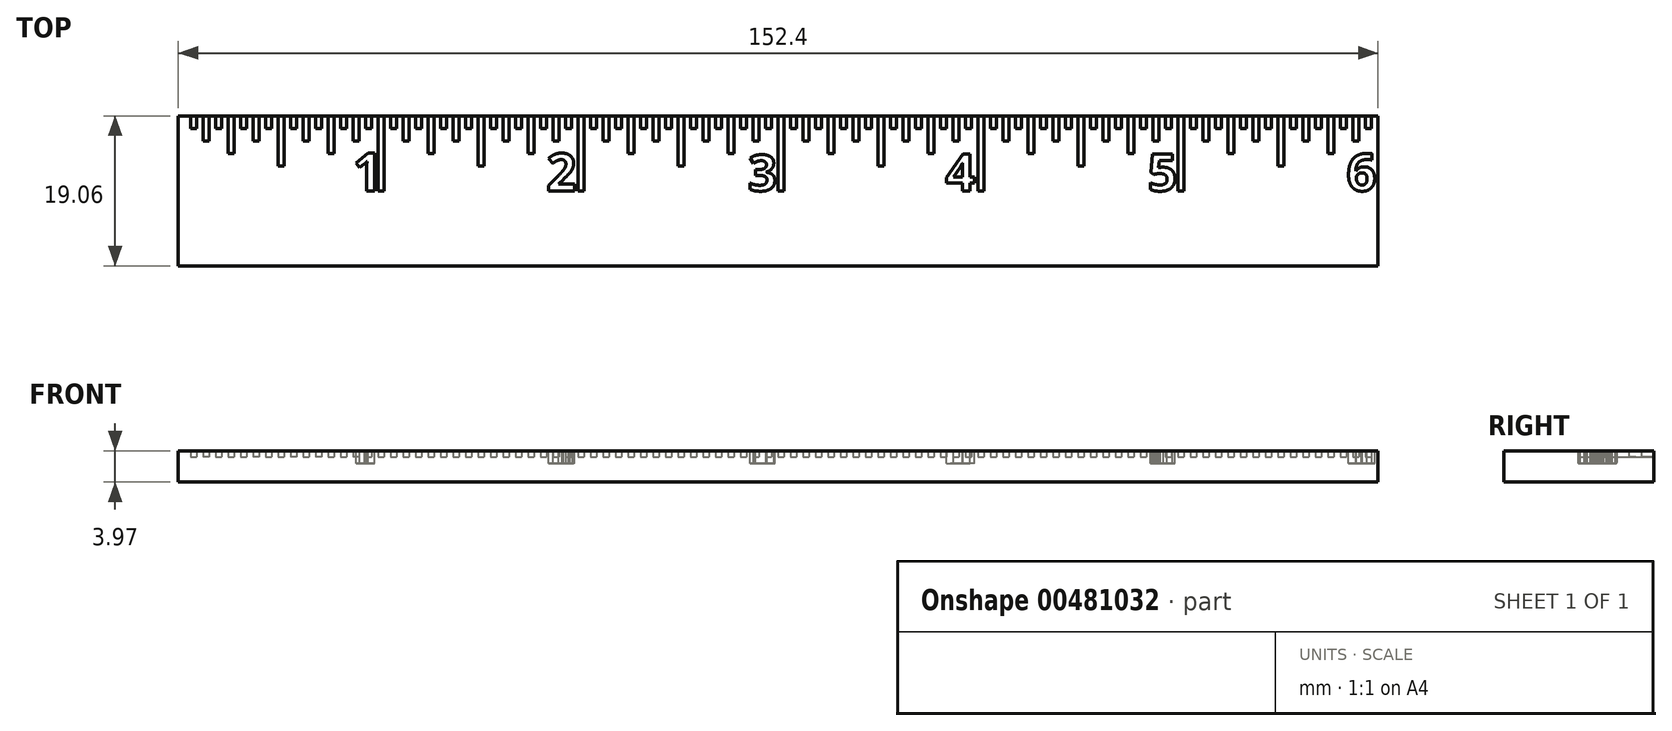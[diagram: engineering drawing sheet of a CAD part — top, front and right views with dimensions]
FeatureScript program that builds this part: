
annotation { "Feature Type Name" : "Feature", "Feature Type Description" : "" }
export const myFeature = defineFeature(function(context is Context, id is Id, definition is map)
    precondition{}
    {
        {
            var Q0;
            Q0=qCreatedBy(makeId("Top.planeOp"),FACE);
            var sketch = newSketch(context, id + "F0", { "sketchPlane" : qUnion([Q0])});
            skLineSegment(sketch, "E0.bottom", {"start": v(-76.2, 9.52) * mm, "end": v(76.2, 9.52) * mm});
            skLineSegment(sketch, "E0.top", {"start": v(-76.2, -9.52) * mm, "end": v(76.2, -9.52) * mm});
            skLineSegment(sketch, "E0.left", {"start": v(-76.2, 9.52) * mm, "end": v(-76.2, -9.52) * mm});
            skLineSegment(sketch, "E0.right", {"start": v(76.2, 9.52) * mm, "end": v(76.2, -9.52) * mm});
            skPoint(sketch, "E0.middle", {"position": v(0, 0) * mm});
            skSolve(sketch);
        }
        {
            var Q0;
            Q0 = qSketchRegion(id + "F0", true);
            extrude(context, id + "F1", {"entities" : qUnion([Q0]), "depth" : 3.17 * mm});
        }
        {
            var Q0;
            Q0=makeQuery(id+"F1.opExtrude","CAP_FACE",FACE,{"disambiguationData":[OSD([sQuery(id+"F0.wireOp",EDGE,"E0.bottom"),sQuery(id+"F0.wireOp",EDGE,"E0.top"),sQuery(id+"F0.wireOp",EDGE,"E0.left"),sQuery(id+"F0.wireOp",EDGE,"E0.right")])],"isStart":false});
            var sketch = newSketch(context, id + "F2", { "sketchPlane" : qUnion([Q0])});
            skLineSegment(sketch, "E1", {"start": v(-50.8, 9.52) * mm, "end": v(-50.8, 0) * mm});
            skLineSegment(sketch, "E2.1.0.0", {"start": v(-25.4, 9.52) * mm, "end": v(-25.4, 0) * mm});
            skLineSegment(sketch, "E2.2.0.0", {"start": v(0, 9.52) * mm, "end": v(0, 0) * mm});
            skLineSegment(sketch, "E2.3.0.0", {"start": v(25.4, 9.52) * mm, "end": v(25.4, 0) * mm});
            skLineSegment(sketch, "E2.4.0.0", {"start": v(50.8, 9.52) * mm, "end": v(50.8, 0) * mm});
            skLineSegment(sketch, "E2.direction1", {"start": v(-50.8, 0) * mm, "end": v(-25.4, 0) * mm, "construction": true});
            skLineSegment(sketch, "E3", {"start": v(-63.5, 9.52) * mm, "end": v(-63.5, 3.17) * mm});
            skLineSegment(sketch, "E4.1.0.0", {"start": v(-38.1, 9.52) * mm, "end": v(-38.1, 3.17) * mm});
            skLineSegment(sketch, "E4.2.0.0", {"start": v(-12.7, 9.52) * mm, "end": v(-12.7, 3.17) * mm});
            skLineSegment(sketch, "E4.3.0.0", {"start": v(12.7, 9.52) * mm, "end": v(12.7, 3.17) * mm});
            skLineSegment(sketch, "E4.4.0.0", {"start": v(38.1, 9.52) * mm, "end": v(38.1, 3.17) * mm});
            skLineSegment(sketch, "E4.5.0.0", {"start": v(63.5, 9.52) * mm, "end": v(63.5, 3.17) * mm});
            skLineSegment(sketch, "E4.direction1", {"start": v(-63.5, 3.17) * mm, "end": v(-38.1, 3.17) * mm, "construction": true});
            skLineSegment(sketch, "E5", {"start": v(-69.85, 9.52) * mm, "end": v(-69.85, 4.76) * mm});
            skLineSegment(sketch, "E6.1.0.0", {"start": v(-57.15, 9.52) * mm, "end": v(-57.15, 4.76) * mm});
            skLineSegment(sketch, "E6.2.0.0", {"start": v(-44.45, 9.52) * mm, "end": v(-44.45, 4.76) * mm});
            skLineSegment(sketch, "E6.3.0.0", {"start": v(-31.75, 9.52) * mm, "end": v(-31.75, 4.76) * mm});
            skLineSegment(sketch, "E6.4.0.0", {"start": v(-19.05, 9.52) * mm, "end": v(-19.05, 4.76) * mm});
            skLineSegment(sketch, "E6.5.0.0", {"start": v(-6.35, 9.52) * mm, "end": v(-6.35, 4.76) * mm});
            skLineSegment(sketch, "E6.6.0.0", {"start": v(6.35, 9.52) * mm, "end": v(6.35, 4.76) * mm});
            skLineSegment(sketch, "E6.7.0.0", {"start": v(19.05, 9.52) * mm, "end": v(19.05, 4.76) * mm});
            skLineSegment(sketch, "E6.8.0.0", {"start": v(31.75, 9.52) * mm, "end": v(31.75, 4.76) * mm});
            skLineSegment(sketch, "E6.9.0.0", {"start": v(44.45, 9.52) * mm, "end": v(44.45, 4.76) * mm});
            skLineSegment(sketch, "E6.10.0.0", {"start": v(57.15, 9.52) * mm, "end": v(57.15, 4.76) * mm});
            skLineSegment(sketch, "E6.11.0.0", {"start": v(69.85, 9.52) * mm, "end": v(69.85, 4.76) * mm});
            skLineSegment(sketch, "E6.direction1", {"start": v(-69.85, 4.76) * mm, "end": v(-57.15, 4.76) * mm, "construction": true});
            skLineSegment(sketch, "E7", {"start": v(-73.03, 9.52) * mm, "end": v(-73.03, 6.35) * mm});
            skLineSegment(sketch, "E8.1.0.0", {"start": v(-66.68, 9.52) * mm, "end": v(-66.68, 6.35) * mm});
            skLineSegment(sketch, "E8.2.0.0", {"start": v(-60.33, 9.52) * mm, "end": v(-60.33, 6.35) * mm});
            skLineSegment(sketch, "E8.3.0.0", {"start": v(-53.98, 9.52) * mm, "end": v(-53.98, 6.35) * mm});
            skLineSegment(sketch, "E8.4.0.0", {"start": v(-47.63, 9.52) * mm, "end": v(-47.63, 6.35) * mm});
            skLineSegment(sketch, "E8.5.0.0", {"start": v(-41.28, 9.52) * mm, "end": v(-41.28, 6.35) * mm});
            skLineSegment(sketch, "E8.6.0.0", {"start": v(-34.93, 9.52) * mm, "end": v(-34.93, 6.35) * mm});
            skLineSegment(sketch, "E8.7.0.0", {"start": v(-28.58, 9.52) * mm, "end": v(-28.58, 6.35) * mm});
            skLineSegment(sketch, "E8.8.0.0", {"start": v(-22.23, 9.52) * mm, "end": v(-22.23, 6.35) * mm});
            skLineSegment(sketch, "E8.9.0.0", {"start": v(-15.88, 9.52) * mm, "end": v(-15.88, 6.35) * mm});
            skLineSegment(sketch, "E8.10.0.0", {"start": v(-9.53, 9.52) * mm, "end": v(-9.53, 6.35) * mm});
            skLineSegment(sketch, "E8.11.0.0", {"start": v(-3.18, 9.52) * mm, "end": v(-3.18, 6.35) * mm});
            skLineSegment(sketch, "E8.12.0.0", {"start": v(3.17, 9.52) * mm, "end": v(3.17, 6.35) * mm});
            skLineSegment(sketch, "E8.13.0.0", {"start": v(9.52, 9.52) * mm, "end": v(9.52, 6.35) * mm});
            skLineSegment(sketch, "E8.14.0.0", {"start": v(15.87, 9.52) * mm, "end": v(15.87, 6.35) * mm});
            skLineSegment(sketch, "E8.15.0.0", {"start": v(22.22, 9.52) * mm, "end": v(22.22, 6.35) * mm});
            skLineSegment(sketch, "E8.16.0.0", {"start": v(28.57, 9.52) * mm, "end": v(28.57, 6.35) * mm});
            skLineSegment(sketch, "E8.17.0.0", {"start": v(34.92, 9.52) * mm, "end": v(34.92, 6.35) * mm});
            skLineSegment(sketch, "E8.18.0.0", {"start": v(41.27, 9.52) * mm, "end": v(41.27, 6.35) * mm});
            skLineSegment(sketch, "E8.19.0.0", {"start": v(47.62, 9.52) * mm, "end": v(47.62, 6.35) * mm});
            skLineSegment(sketch, "E8.20.0.0", {"start": v(53.97, 9.52) * mm, "end": v(53.97, 6.35) * mm});
            skLineSegment(sketch, "E8.21.0.0", {"start": v(60.32, 9.52) * mm, "end": v(60.32, 6.35) * mm});
            skLineSegment(sketch, "E8.22.0.0", {"start": v(66.67, 9.52) * mm, "end": v(66.67, 6.35) * mm});
            skLineSegment(sketch, "E8.23.0.0", {"start": v(73.02, 9.52) * mm, "end": v(73.02, 6.35) * mm});
            skLineSegment(sketch, "E8.direction1", {"start": v(-73.03, 6.35) * mm, "end": v(-66.68, 6.35) * mm, "construction": true});
            skLineSegment(sketch, "E9", {"start": v(-74.61, 9.52) * mm, "end": v(-74.61, 7.94) * mm});
            skLineSegment(sketch, "E10.1.0.0", {"start": v(-71.44, 9.52) * mm, "end": v(-71.44, 7.94) * mm});
            skLineSegment(sketch, "E10.2.0.0", {"start": v(-68.26, 9.52) * mm, "end": v(-68.26, 7.94) * mm});
            skLineSegment(sketch, "E10.3.0.0", {"start": v(-65.09, 9.52) * mm, "end": v(-65.09, 7.94) * mm});
            skLineSegment(sketch, "E10.4.0.0", {"start": v(-61.91, 9.52) * mm, "end": v(-61.91, 7.94) * mm});
            skLineSegment(sketch, "E10.5.0.0", {"start": v(-58.74, 9.52) * mm, "end": v(-58.74, 7.94) * mm});
            skLineSegment(sketch, "E10.6.0.0", {"start": v(-55.56, 9.52) * mm, "end": v(-55.56, 7.94) * mm});
            skLineSegment(sketch, "E10.7.0.0", {"start": v(-52.39, 9.52) * mm, "end": v(-52.39, 7.94) * mm});
            skLineSegment(sketch, "E10.8.0.0", {"start": v(-49.21, 9.52) * mm, "end": v(-49.21, 7.94) * mm});
            skLineSegment(sketch, "E10.9.0.0", {"start": v(-46.04, 9.52) * mm, "end": v(-46.04, 7.94) * mm});
            skLineSegment(sketch, "E10.10.0.0", {"start": v(-42.86, 9.52) * mm, "end": v(-42.86, 7.94) * mm});
            skLineSegment(sketch, "E10.11.0.0", {"start": v(-39.69, 9.52) * mm, "end": v(-39.69, 7.94) * mm});
            skLineSegment(sketch, "E10.12.0.0", {"start": v(-36.51, 9.52) * mm, "end": v(-36.51, 7.94) * mm});
            skLineSegment(sketch, "E10.13.0.0", {"start": v(-33.34, 9.52) * mm, "end": v(-33.34, 7.94) * mm});
            skLineSegment(sketch, "E10.14.0.0", {"start": v(-30.16, 9.52) * mm, "end": v(-30.16, 7.94) * mm});
            skLineSegment(sketch, "E10.15.0.0", {"start": v(-26.99, 9.52) * mm, "end": v(-26.99, 7.94) * mm});
            skLineSegment(sketch, "E10.16.0.0", {"start": v(-23.81, 9.52) * mm, "end": v(-23.81, 7.94) * mm});
            skLineSegment(sketch, "E10.17.0.0", {"start": v(-20.64, 9.52) * mm, "end": v(-20.64, 7.94) * mm});
            skLineSegment(sketch, "E10.18.0.0", {"start": v(-17.46, 9.52) * mm, "end": v(-17.46, 7.94) * mm});
            skLineSegment(sketch, "E10.19.0.0", {"start": v(-14.29, 9.52) * mm, "end": v(-14.29, 7.94) * mm});
            skLineSegment(sketch, "E10.20.0.0", {"start": v(-11.11, 9.52) * mm, "end": v(-11.11, 7.94) * mm});
            skLineSegment(sketch, "E10.21.0.0", {"start": v(-7.94, 9.52) * mm, "end": v(-7.94, 7.94) * mm});
            skLineSegment(sketch, "E10.22.0.0", {"start": v(-4.76, 9.52) * mm, "end": v(-4.76, 7.94) * mm});
            skLineSegment(sketch, "E10.23.0.0", {"start": v(-1.59, 9.52) * mm, "end": v(-1.59, 7.94) * mm});
            skLineSegment(sketch, "E10.24.0.0", {"start": v(1.59, 9.52) * mm, "end": v(1.59, 7.94) * mm});
            skLineSegment(sketch, "E10.25.0.0", {"start": v(4.76, 9.52) * mm, "end": v(4.76, 7.94) * mm});
            skLineSegment(sketch, "E10.26.0.0", {"start": v(7.94, 9.52) * mm, "end": v(7.94, 7.94) * mm});
            skLineSegment(sketch, "E10.27.0.0", {"start": v(11.11, 9.52) * mm, "end": v(11.11, 7.94) * mm});
            skLineSegment(sketch, "E10.28.0.0", {"start": v(14.29, 9.52) * mm, "end": v(14.29, 7.94) * mm});
            skLineSegment(sketch, "E10.29.0.0", {"start": v(17.46, 9.52) * mm, "end": v(17.46, 7.94) * mm});
            skLineSegment(sketch, "E10.30.0.0", {"start": v(20.64, 9.52) * mm, "end": v(20.64, 7.94) * mm});
            skLineSegment(sketch, "E10.31.0.0", {"start": v(23.81, 9.52) * mm, "end": v(23.81, 7.94) * mm});
            skLineSegment(sketch, "E10.32.0.0", {"start": v(26.99, 9.52) * mm, "end": v(26.99, 7.94) * mm});
            skLineSegment(sketch, "E10.33.0.0", {"start": v(30.16, 9.52) * mm, "end": v(30.16, 7.94) * mm});
            skLineSegment(sketch, "E10.34.0.0", {"start": v(33.34, 9.52) * mm, "end": v(33.34, 7.94) * mm});
            skLineSegment(sketch, "E10.35.0.0", {"start": v(36.51, 9.52) * mm, "end": v(36.51, 7.94) * mm});
            skLineSegment(sketch, "E10.36.0.0", {"start": v(39.69, 9.52) * mm, "end": v(39.69, 7.94) * mm});
            skLineSegment(sketch, "E10.37.0.0", {"start": v(42.86, 9.52) * mm, "end": v(42.86, 7.94) * mm});
            skLineSegment(sketch, "E10.38.0.0", {"start": v(46.04, 9.52) * mm, "end": v(46.04, 7.94) * mm});
            skLineSegment(sketch, "E10.39.0.0", {"start": v(49.21, 9.52) * mm, "end": v(49.21, 7.94) * mm});
            skLineSegment(sketch, "E10.40.0.0", {"start": v(52.39, 9.52) * mm, "end": v(52.39, 7.94) * mm});
            skLineSegment(sketch, "E10.41.0.0", {"start": v(55.56, 9.52) * mm, "end": v(55.56, 7.94) * mm});
            skLineSegment(sketch, "E10.42.0.0", {"start": v(58.74, 9.52) * mm, "end": v(58.74, 7.94) * mm});
            skLineSegment(sketch, "E10.43.0.0", {"start": v(61.91, 9.52) * mm, "end": v(61.91, 7.94) * mm});
            skLineSegment(sketch, "E10.44.0.0", {"start": v(65.09, 9.52) * mm, "end": v(65.09, 7.94) * mm});
            skLineSegment(sketch, "E10.45.0.0", {"start": v(68.26, 9.52) * mm, "end": v(68.26, 7.94) * mm});
            skLineSegment(sketch, "E10.46.0.0", {"start": v(71.44, 9.52) * mm, "end": v(71.44, 7.94) * mm});
            skLineSegment(sketch, "E10.47.0.0", {"start": v(74.61, 9.52) * mm, "end": v(74.61, 7.94) * mm});
            skLineSegment(sketch, "E10.direction1", {"start": v(-74.61, 7.94) * mm, "end": v(-71.44, 7.94) * mm, "construction": true});
            skLineSegment(sketch, "E11.0", {"start": v(-82.55, 15.87) * mm, "end": v(-82.55, -15.87) * mm});
            skLineSegment(sketch, "E11.1", {"start": v(82.55, 15.87) * mm, "end": v(-82.55, 15.87) * mm});
            skLineSegment(sketch, "E11.2", {"start": v(82.55, -15.87) * mm, "end": v(82.55, 15.87) * mm});
            skLineSegment(sketch, "E11.3", {"start": v(-82.55, -15.87) * mm, "end": v(82.55, -15.87) * mm});
            skLineSegment(sketch, "E12.MirrorCS", {"start": v(74.61, 9.53) * mm, "end": v(74.61, 7.94) * mm});
            skLineSegment(sketch, "E13.MirrorCS", {"start": v(71.44, 9.53) * mm, "end": v(71.44, 7.94) * mm});
            skLineSegment(sketch, "E14.MirrorCS", {"start": v(68.26, 9.53) * mm, "end": v(68.26, 7.94) * mm});
            skLineSegment(sketch, "E15.MirrorCS", {"start": v(65.09, 9.53) * mm, "end": v(65.09, 7.94) * mm});
            skLineSegment(sketch, "E16.MirrorCS", {"start": v(61.91, 9.53) * mm, "end": v(61.91, 7.94) * mm});
            skLineSegment(sketch, "E17.MirrorCS", {"start": v(58.74, 9.53) * mm, "end": v(58.74, 7.94) * mm});
            skLineSegment(sketch, "E18.MirrorCS", {"start": v(55.56, 9.53) * mm, "end": v(55.56, 7.94) * mm});
            skLineSegment(sketch, "E19.MirrorCS", {"start": v(73.03, 9.53) * mm, "end": v(73.03, 6.35) * mm});
            skLineSegment(sketch, "E20.MirrorCS", {"start": v(69.85, 9.53) * mm, "end": v(69.85, 4.76) * mm});
            skLineSegment(sketch, "E21.MirrorCS", {"start": v(66.68, 9.53) * mm, "end": v(66.68, 6.35) * mm});
            skLineSegment(sketch, "E22.MirrorCS", {"start": v(30.16, 9.53) * mm, "end": v(30.16, 7.94) * mm});
            skLineSegment(sketch, "E23.MirrorCS", {"start": v(31.75, 9.53) * mm, "end": v(31.75, 4.76) * mm});
            skLineSegment(sketch, "E24.MirrorCS", {"start": v(33.34, 9.53) * mm, "end": v(33.34, 7.94) * mm});
            skLineSegment(sketch, "E25.MirrorCS", {"start": v(34.93, 9.53) * mm, "end": v(34.93, 6.35) * mm});
            skLineSegment(sketch, "E26.MirrorCS", {"start": v(36.51, 9.53) * mm, "end": v(36.51, 7.94) * mm});
            skLineSegment(sketch, "E27.MirrorCS", {"start": v(38.1, 9.53) * mm, "end": v(38.1, 3.18) * mm});
            skLineSegment(sketch, "E28.MirrorCS", {"start": v(39.69, 9.53) * mm, "end": v(39.69, 7.94) * mm});
            skLineSegment(sketch, "E29.MirrorCS", {"start": v(41.28, 9.53) * mm, "end": v(41.28, 6.35) * mm});
            skLineSegment(sketch, "E30.MirrorCS", {"start": v(42.86, 9.53) * mm, "end": v(42.86, 7.94) * mm});
            skLineSegment(sketch, "E31.MirrorCS", {"start": v(44.45, 9.53) * mm, "end": v(44.45, 4.76) * mm});
            skLineSegment(sketch, "E32.MirrorCS", {"start": v(46.04, 9.53) * mm, "end": v(46.04, 7.94) * mm});
            skLineSegment(sketch, "E33.MirrorCS", {"start": v(47.63, 9.53) * mm, "end": v(47.63, 6.35) * mm});
            skLineSegment(sketch, "E34.MirrorCS", {"start": v(49.21, 9.53) * mm, "end": v(49.21, 7.94) * mm});
            skLineSegment(sketch, "E35.MirrorCS", {"start": v(52.39, 9.53) * mm, "end": v(52.39, 7.94) * mm});
            skLineSegment(sketch, "E36.MirrorCS", {"start": v(53.98, 9.53) * mm, "end": v(53.98, 6.35) * mm});
            skLineSegment(sketch, "E37.MirrorCS", {"start": v(57.15, 9.53) * mm, "end": v(57.15, 4.76) * mm});
            skLineSegment(sketch, "E38", {"start": v(-73.85, 9.52) * mm, "end": v(-73.85, 7.94) * mm});
            skLineSegment(sketch, "E39", {"start": v(-73.85, 7.94) * mm, "end": v(-74.61, 7.94) * mm});
            skLineSegment(sketch, "E40", {"start": v(-73.85, 9.52) * mm, "end": v(-74.61, 9.52) * mm});
            skLineSegment(sketch, "E41", {"start": v(-72.26, 9.52) * mm, "end": v(-72.26, 6.35) * mm});
            skLineSegment(sketch, "E42", {"start": v(-72.26, 6.35) * mm, "end": v(-73.03, 6.35) * mm});
            skLineSegment(sketch, "E43", {"start": v(-73.03, 9.52) * mm, "end": v(-72.26, 9.52) * mm});
            skLineSegment(sketch, "E44", {"start": v(-71.44, 9.52) * mm, "end": v(-71.2, 9.52) * mm});
            skLineSegment(sketch, "E45", {"start": v(-71.2, 6.35) * mm, "end": v(-71.44, 6.35) * mm});
            skLineSegment(sketch, "E46", {"start": v(-69.09, 4.76) * mm, "end": v(-69.09, 9.52) * mm});
            skLineSegment(sketch, "E47", {"start": v(-69.09, 9.52) * mm, "end": v(-69.85, 9.52) * mm});
            skLineSegment(sketch, "E48", {"start": v(-69.85, 4.76) * mm, "end": v(-69.09, 4.76) * mm});
            skLineSegment(sketch, "E49", {"start": v(-62.74, 3.17) * mm, "end": v(-62.74, 9.52) * mm});
            skLineSegment(sketch, "E50", {"start": v(-62.74, 9.52) * mm, "end": v(-63.5, 9.52) * mm});
            skLineSegment(sketch, "E51", {"start": v(-63.5, 3.17) * mm, "end": v(-62.74, 3.17) * mm});
            skLineSegment(sketch, "E52.1.0.0", {"start": v(-70.68, 9.52) * mm, "end": v(-70.68, 7.94) * mm});
            skLineSegment(sketch, "E52.2.0.0", {"start": v(-67.5, 9.52) * mm, "end": v(-67.5, 7.94) * mm});
            skLineSegment(sketch, "E52.3.0.0", {"start": v(-64.33, 9.52) * mm, "end": v(-64.33, 7.94) * mm});
            skLineSegment(sketch, "E52.4.0.0", {"start": v(-61.15, 9.52) * mm, "end": v(-61.15, 7.94) * mm});
            skLineSegment(sketch, "E52.5.0.0", {"start": v(-57.98, 9.52) * mm, "end": v(-57.98, 7.94) * mm});
            skLineSegment(sketch, "E52.6.0.0", {"start": v(-54.8, 9.52) * mm, "end": v(-54.8, 7.94) * mm});
            skLineSegment(sketch, "E52.7.0.0", {"start": v(-51.63, 9.52) * mm, "end": v(-51.63, 7.94) * mm});
            skLineSegment(sketch, "E52.8.0.0", {"start": v(-48.45, 9.52) * mm, "end": v(-48.45, 7.94) * mm});
            skLineSegment(sketch, "E52.9.0.0", {"start": v(-45.28, 9.52) * mm, "end": v(-45.28, 7.94) * mm});
            skLineSegment(sketch, "E52.10.0.0", {"start": v(-42.1, 9.52) * mm, "end": v(-42.1, 7.94) * mm});
            skLineSegment(sketch, "E52.11.0.0", {"start": v(-38.93, 9.52) * mm, "end": v(-38.93, 7.94) * mm});
            skLineSegment(sketch, "E52.12.0.0", {"start": v(-35.75, 9.52) * mm, "end": v(-35.75, 7.94) * mm});
            skLineSegment(sketch, "E52.13.0.0", {"start": v(-32.58, 9.52) * mm, "end": v(-32.58, 7.94) * mm});
            skLineSegment(sketch, "E52.14.0.0", {"start": v(-29.4, 9.52) * mm, "end": v(-29.4, 7.94) * mm});
            skLineSegment(sketch, "E52.15.0.0", {"start": v(-26.23, 9.52) * mm, "end": v(-26.23, 7.94) * mm});
            skLineSegment(sketch, "E52.16.0.0", {"start": v(-23.05, 9.52) * mm, "end": v(-23.05, 7.94) * mm});
            skLineSegment(sketch, "E52.17.0.0", {"start": v(-19.88, 9.52) * mm, "end": v(-19.88, 7.94) * mm});
            skLineSegment(sketch, "E52.18.0.0", {"start": v(-16.7, 9.52) * mm, "end": v(-16.7, 7.94) * mm});
            skLineSegment(sketch, "E52.19.0.0", {"start": v(-13.53, 9.52) * mm, "end": v(-13.53, 7.94) * mm});
            skLineSegment(sketch, "E52.20.0.0", {"start": v(-10.35, 9.52) * mm, "end": v(-10.35, 7.94) * mm});
            skLineSegment(sketch, "E52.21.0.0", {"start": v(-7.18, 9.52) * mm, "end": v(-7.18, 7.94) * mm});
            skLineSegment(sketch, "E52.22.0.0", {"start": v(-4, 9.52) * mm, "end": v(-4, 7.94) * mm});
            skLineSegment(sketch, "E52.23.0.0", {"start": v(-0.83, 9.52) * mm, "end": v(-0.83, 7.94) * mm});
            skLineSegment(sketch, "E52.24.0.0", {"start": v(2.35, 9.52) * mm, "end": v(2.35, 7.94) * mm});
            skLineSegment(sketch, "E52.25.0.0", {"start": v(5.52, 9.52) * mm, "end": v(5.52, 7.94) * mm});
            skLineSegment(sketch, "E52.26.0.0", {"start": v(8.7, 9.52) * mm, "end": v(8.7, 7.94) * mm});
            skLineSegment(sketch, "E52.27.0.0", {"start": v(11.87, 9.52) * mm, "end": v(11.87, 7.94) * mm});
            skLineSegment(sketch, "E52.28.0.0", {"start": v(15.05, 9.52) * mm, "end": v(15.05, 7.94) * mm});
            skLineSegment(sketch, "E52.29.0.0", {"start": v(18.22, 9.52) * mm, "end": v(18.22, 7.94) * mm});
            skLineSegment(sketch, "E52.30.0.0", {"start": v(21.4, 9.52) * mm, "end": v(21.4, 7.94) * mm});
            skLineSegment(sketch, "E52.31.0.0", {"start": v(24.57, 9.52) * mm, "end": v(24.57, 7.94) * mm});
            skLineSegment(sketch, "E52.32.0.0", {"start": v(27.75, 9.52) * mm, "end": v(27.75, 7.94) * mm});
            skLineSegment(sketch, "E52.33.0.0", {"start": v(30.92, 9.52) * mm, "end": v(30.92, 7.94) * mm});
            skLineSegment(sketch, "E52.34.0.0", {"start": v(34.1, 9.52) * mm, "end": v(34.1, 7.94) * mm});
            skLineSegment(sketch, "E52.35.0.0", {"start": v(37.27, 9.52) * mm, "end": v(37.27, 7.94) * mm});
            skLineSegment(sketch, "E52.36.0.0", {"start": v(40.45, 9.52) * mm, "end": v(40.45, 7.94) * mm});
            skLineSegment(sketch, "E52.37.0.0", {"start": v(43.62, 9.52) * mm, "end": v(43.62, 7.94) * mm});
            skLineSegment(sketch, "E52.38.0.0", {"start": v(46.8, 9.52) * mm, "end": v(46.8, 7.94) * mm});
            skLineSegment(sketch, "E52.39.0.0", {"start": v(49.97, 9.52) * mm, "end": v(49.97, 7.94) * mm});
            skLineSegment(sketch, "E52.40.0.0", {"start": v(53.15, 9.52) * mm, "end": v(53.15, 7.94) * mm});
            skLineSegment(sketch, "E52.41.0.0", {"start": v(56.32, 9.52) * mm, "end": v(56.32, 7.94) * mm});
            skLineSegment(sketch, "E52.42.0.0", {"start": v(59.5, 9.52) * mm, "end": v(59.5, 7.94) * mm});
            skLineSegment(sketch, "E52.43.0.0", {"start": v(62.67, 9.52) * mm, "end": v(62.67, 7.94) * mm});
            skLineSegment(sketch, "E52.44.0.0", {"start": v(65.85, 9.52) * mm, "end": v(65.85, 7.94) * mm});
            skLineSegment(sketch, "E52.45.0.0", {"start": v(69.02, 9.52) * mm, "end": v(69.02, 7.94) * mm});
            skLineSegment(sketch, "E52.46.0.0", {"start": v(72.2, 9.52) * mm, "end": v(72.2, 7.94) * mm});
            skLineSegment(sketch, "E52.47.0.0", {"start": v(75.37, 9.52) * mm, "end": v(75.37, 7.94) * mm});
            skLineSegment(sketch, "E52.direction1", {"start": v(-73.85, 7.94) * mm, "end": v(-70.68, 7.94) * mm, "construction": true});
            skLineSegment(sketch, "E53.1.0.0", {"start": v(-65.91, 9.52) * mm, "end": v(-65.91, 6.35) * mm});
            skLineSegment(sketch, "E53.2.0.0", {"start": v(-59.56, 9.52) * mm, "end": v(-59.56, 6.35) * mm});
            skLineSegment(sketch, "E53.3.0.0", {"start": v(-53.21, 9.52) * mm, "end": v(-53.21, 6.35) * mm});
            skLineSegment(sketch, "E53.4.0.0", {"start": v(-46.86, 9.52) * mm, "end": v(-46.86, 6.35) * mm});
            skLineSegment(sketch, "E53.5.0.0", {"start": v(-40.51, 9.52) * mm, "end": v(-40.51, 6.35) * mm});
            skLineSegment(sketch, "E53.6.0.0", {"start": v(-34.16, 9.52) * mm, "end": v(-34.16, 6.35) * mm});
            skLineSegment(sketch, "E53.7.0.0", {"start": v(-27.81, 9.52) * mm, "end": v(-27.81, 6.35) * mm});
            skLineSegment(sketch, "E53.8.0.0", {"start": v(-21.46, 9.52) * mm, "end": v(-21.46, 6.35) * mm});
            skLineSegment(sketch, "E53.9.0.0", {"start": v(-15.11, 9.52) * mm, "end": v(-15.11, 6.35) * mm});
            skLineSegment(sketch, "E53.10.0.0", {"start": v(-8.76, 9.52) * mm, "end": v(-8.76, 6.35) * mm});
            skLineSegment(sketch, "E53.11.0.0", {"start": v(-2.41, 9.52) * mm, "end": v(-2.41, 6.35) * mm});
            skLineSegment(sketch, "E53.12.0.0", {"start": v(3.94, 9.52) * mm, "end": v(3.94, 6.35) * mm});
            skLineSegment(sketch, "E53.13.0.0", {"start": v(10.29, 9.52) * mm, "end": v(10.29, 6.35) * mm});
            skLineSegment(sketch, "E53.14.0.0", {"start": v(16.64, 9.52) * mm, "end": v(16.64, 6.35) * mm});
            skLineSegment(sketch, "E53.15.0.0", {"start": v(22.99, 9.52) * mm, "end": v(22.99, 6.35) * mm});
            skLineSegment(sketch, "E53.16.0.0", {"start": v(29.34, 9.52) * mm, "end": v(29.34, 6.35) * mm});
            skLineSegment(sketch, "E53.17.0.0", {"start": v(35.69, 9.52) * mm, "end": v(35.69, 6.35) * mm});
            skLineSegment(sketch, "E53.18.0.0", {"start": v(42.04, 9.52) * mm, "end": v(42.04, 6.35) * mm});
            skLineSegment(sketch, "E53.19.0.0", {"start": v(48.39, 9.52) * mm, "end": v(48.39, 6.35) * mm});
            skLineSegment(sketch, "E53.20.0.0", {"start": v(54.74, 9.52) * mm, "end": v(54.74, 6.35) * mm});
            skLineSegment(sketch, "E53.21.0.0", {"start": v(61.09, 9.52) * mm, "end": v(61.09, 6.35) * mm});
            skLineSegment(sketch, "E53.22.0.0", {"start": v(67.44, 9.52) * mm, "end": v(67.44, 6.35) * mm});
            skLineSegment(sketch, "E53.23.0.0", {"start": v(73.79, 9.52) * mm, "end": v(73.79, 6.35) * mm});
            skLineSegment(sketch, "E53.direction1", {"start": v(-72.26, 6.35) * mm, "end": v(-65.91, 6.35) * mm, "construction": true});
            skLineSegment(sketch, "E54.1.0.0", {"start": v(-56.39, 4.76) * mm, "end": v(-56.39, 9.52) * mm});
            skLineSegment(sketch, "E54.2.0.0", {"start": v(-43.69, 4.76) * mm, "end": v(-43.69, 9.52) * mm});
            skLineSegment(sketch, "E54.3.0.0", {"start": v(-30.99, 4.76) * mm, "end": v(-30.99, 9.52) * mm});
            skLineSegment(sketch, "E54.4.0.0", {"start": v(-18.29, 4.76) * mm, "end": v(-18.29, 9.52) * mm});
            skLineSegment(sketch, "E54.5.0.0", {"start": v(-5.59, 4.76) * mm, "end": v(-5.59, 9.52) * mm});
            skLineSegment(sketch, "E54.6.0.0", {"start": v(7.11, 4.76) * mm, "end": v(7.11, 9.52) * mm});
            skLineSegment(sketch, "E54.7.0.0", {"start": v(19.81, 4.76) * mm, "end": v(19.81, 9.52) * mm});
            skLineSegment(sketch, "E54.8.0.0", {"start": v(32.51, 4.76) * mm, "end": v(32.51, 9.52) * mm});
            skLineSegment(sketch, "E54.9.0.0", {"start": v(45.21, 4.76) * mm, "end": v(45.21, 9.52) * mm});
            skLineSegment(sketch, "E54.10.0.0", {"start": v(57.91, 4.76) * mm, "end": v(57.91, 9.52) * mm});
            skLineSegment(sketch, "E54.11.0.0", {"start": v(70.61, 4.76) * mm, "end": v(70.61, 9.52) * mm});
            skLineSegment(sketch, "E54.direction1", {"start": v(-69.09, 4.76) * mm, "end": v(-56.39, 4.76) * mm, "construction": true});
            skLineSegment(sketch, "E55", {"start": v(-68.26, 7.94) * mm, "end": v(-67.5, 7.94) * mm});
            skLineSegment(sketch, "E56", {"start": v(-71.44, 7.94) * mm, "end": v(-70.68, 7.94) * mm});
            skLineSegment(sketch, "E57", {"start": v(-65.09, 9.52) * mm, "end": v(-64.33, 9.52) * mm});
            skLineSegment(sketch, "E58", {"start": v(-65.09, 7.94) * mm, "end": v(-64.33, 7.94) * mm});
            skLineSegment(sketch, "E59", {"start": v(-64.84, 9.52) * mm, "end": v(-65.09, 9.52) * mm});
            skLineSegment(sketch, "E60", {"start": v(-66.68, 9.52) * mm, "end": v(-65.91, 9.52) * mm});
            skLineSegment(sketch, "E61", {"start": v(-65.91, 6.35) * mm, "end": v(-66.68, 6.35) * mm});
            skLineSegment(sketch, "E62", {"start": v(-61.91, 9.52) * mm, "end": v(-61.15, 9.52) * mm});
            skLineSegment(sketch, "E63", {"start": v(-61.15, 7.94) * mm, "end": v(-61.91, 7.94) * mm});
            skLineSegment(sketch, "E64", {"start": v(-60.33, 6.35) * mm, "end": v(-59.56, 6.35) * mm});
            skLineSegment(sketch, "E65", {"start": v(-60.33, 9.52) * mm, "end": v(-59.56, 9.52) * mm});
            skLineSegment(sketch, "E66", {"start": v(-58.74, 9.52) * mm, "end": v(-57.98, 9.52) * mm});
            skLineSegment(sketch, "E67", {"start": v(-57.98, 7.94) * mm, "end": v(-58.74, 7.94) * mm});
            skLineSegment(sketch, "E68", {"start": v(-57.15, 9.52) * mm, "end": v(-56.39, 9.52) * mm});
            skLineSegment(sketch, "E69", {"start": v(-56.39, 4.76) * mm, "end": v(-57.15, 4.76) * mm});
            skLineSegment(sketch, "E70", {"start": v(-55.56, 7.94) * mm, "end": v(-54.8, 7.94) * mm});
            skLineSegment(sketch, "E71", {"start": v(-55.56, 9.52) * mm, "end": v(-54.8, 9.52) * mm});
            skLineSegment(sketch, "E72", {"start": v(-53.98, 9.52) * mm, "end": v(-53.21, 9.52) * mm});
            skLineSegment(sketch, "E73", {"start": v(-53.21, 6.35) * mm, "end": v(-53.98, 6.35) * mm});
            skLineSegment(sketch, "E74", {"start": v(-52.39, 7.94) * mm, "end": v(-51.63, 7.94) * mm});
            skLineSegment(sketch, "E75", {"start": v(-49.21, 7.94) * mm, "end": v(-48.45, 7.94) * mm});
            skLineSegment(sketch, "E76.1.0.0", {"start": v(-37.34, 3.17) * mm, "end": v(-37.34, 9.52) * mm});
            skLineSegment(sketch, "E76.2.0.0", {"start": v(-11.94, 3.17) * mm, "end": v(-11.94, 9.52) * mm});
            skLineSegment(sketch, "E76.3.0.0", {"start": v(13.46, 3.17) * mm, "end": v(13.46, 9.52) * mm});
            skLineSegment(sketch, "E76.4.0.0", {"start": v(38.86, 3.17) * mm, "end": v(38.86, 9.52) * mm});
            skLineSegment(sketch, "E76.5.0.0", {"start": v(64.26, 3.17) * mm, "end": v(64.26, 9.52) * mm});
            skLineSegment(sketch, "E76.direction1", {"start": v(-63, 3.17) * mm, "end": v(-37.6, 3.17) * mm, "construction": true});
            skLineSegment(sketch, "E77", {"start": v(-50.04, 0) * mm, "end": v(-50.04, 9.52) * mm});
            skLineSegment(sketch, "E78", {"start": v(-50.8, 9.52) * mm, "end": v(-50.04, 9.52) * mm});
            skLineSegment(sketch, "E79", {"start": v(-50.04, 0) * mm, "end": v(-50.8, 0) * mm});
            skLineSegment(sketch, "E80.1.0.0", {"start": v(-24.64, 0) * mm, "end": v(-24.64, 9.52) * mm});
            skLineSegment(sketch, "E80.2.0.0", {"start": v(0.76, 0) * mm, "end": v(0.76, 9.52) * mm});
            skLineSegment(sketch, "E80.3.0.0", {"start": v(26.16, 0) * mm, "end": v(26.16, 9.52) * mm});
            skLineSegment(sketch, "E80.4.0.0", {"start": v(51.56, 0) * mm, "end": v(51.56, 9.52) * mm});
            skLineSegment(sketch, "E80.direction1", {"start": v(-50.04, 0) * mm, "end": v(-24.64, 0) * mm, "construction": true});
            skLineSegment(sketch, "E81", {"start": v(-47.63, 6.35) * mm, "end": v(-46.86, 6.35) * mm});
            skLineSegment(sketch, "E82", {"start": v(-46.04, 7.94) * mm, "end": v(-45.28, 7.94) * mm});
            skLineSegment(sketch, "E83", {"start": v(-44.45, 4.76) * mm, "end": v(-43.69, 4.76) * mm});
            skLineSegment(sketch, "E84", {"start": v(-42.86, 7.94) * mm, "end": v(-42.1, 7.94) * mm});
            skLineSegment(sketch, "E85", {"start": v(-41.28, 6.35) * mm, "end": v(-40.51, 6.35) * mm});
            skLineSegment(sketch, "E86", {"start": v(-39.69, 7.94) * mm, "end": v(-38.93, 7.94) * mm});
            skLineSegment(sketch, "E87", {"start": v(-38.1, 3.17) * mm, "end": v(-37.34, 3.17) * mm});
            skLineSegment(sketch, "E88", {"start": v(-36.51, 7.94) * mm, "end": v(-35.75, 7.94) * mm});
            skLineSegment(sketch, "E89", {"start": v(-34.93, 6.35) * mm, "end": v(-34.16, 6.35) * mm});
            skLineSegment(sketch, "E90", {"start": v(-33.34, 7.94) * mm, "end": v(-32.58, 7.94) * mm});
            skLineSegment(sketch, "E91", {"start": v(-31.75, 4.76) * mm, "end": v(-30.99, 4.76) * mm});
            skLineSegment(sketch, "E92", {"start": v(-30.16, 7.94) * mm, "end": v(-29.4, 7.94) * mm});
            skLineSegment(sketch, "E93", {"start": v(-28.58, 6.35) * mm, "end": v(-27.81, 6.35) * mm});
            skLineSegment(sketch, "E94", {"start": v(-26.99, 7.94) * mm, "end": v(-26.23, 7.94) * mm});
            skLineSegment(sketch, "E95", {"start": v(-25.4, 0) * mm, "end": v(-24.64, 0) * mm});
            skLineSegment(sketch, "E96", {"start": v(-23.81, 7.94) * mm, "end": v(-23.05, 7.94) * mm});
            skLineSegment(sketch, "E97", {"start": v(-22.23, 6.35) * mm, "end": v(-21.46, 6.35) * mm});
            skLineSegment(sketch, "E98", {"start": v(-20.64, 7.94) * mm, "end": v(-19.88, 7.94) * mm});
            skLineSegment(sketch, "E99", {"start": v(-19.05, 4.76) * mm, "end": v(-18.29, 4.76) * mm});
            skLineSegment(sketch, "E100", {"start": v(-17.46, 7.94) * mm, "end": v(-16.7, 7.94) * mm});
            skLineSegment(sketch, "E101", {"start": v(-15.88, 6.35) * mm, "end": v(-15.11, 6.35) * mm});
            skLineSegment(sketch, "E102", {"start": v(-14.29, 7.94) * mm, "end": v(-13.53, 7.94) * mm});
            skLineSegment(sketch, "E103", {"start": v(-12.7, 3.17) * mm, "end": v(-11.94, 3.17) * mm});
            skLineSegment(sketch, "E104", {"start": v(-11.11, 7.94) * mm, "end": v(-10.35, 7.94) * mm});
            skLineSegment(sketch, "E105", {"start": v(-9.53, 6.35) * mm, "end": v(-8.76, 6.35) * mm});
            skLineSegment(sketch, "E106", {"start": v(-7.94, 7.94) * mm, "end": v(-7.18, 7.94) * mm});
            skLineSegment(sketch, "E107", {"start": v(-6.35, 4.76) * mm, "end": v(-5.59, 4.76) * mm});
            skLineSegment(sketch, "E108", {"start": v(-4.76, 7.94) * mm, "end": v(-4, 7.94) * mm});
            skLineSegment(sketch, "E109", {"start": v(-3.18, 6.35) * mm, "end": v(-2.41, 6.35) * mm});
            skLineSegment(sketch, "E110", {"start": v(-1.59, 7.94) * mm, "end": v(-0.83, 7.94) * mm});
            skLineSegment(sketch, "E111", {"start": v(0, 0) * mm, "end": v(0.76, 0) * mm});
            skLineSegment(sketch, "E112", {"start": v(1.59, 7.94) * mm, "end": v(2.35, 7.94) * mm});
            skLineSegment(sketch, "E113", {"start": v(3.17, 6.35) * mm, "end": v(3.94, 6.35) * mm});
            skLineSegment(sketch, "E114", {"start": v(4.76, 7.94) * mm, "end": v(5.52, 7.94) * mm});
            skLineSegment(sketch, "E115", {"start": v(6.35, 4.76) * mm, "end": v(7.11, 4.76) * mm});
            skLineSegment(sketch, "E116", {"start": v(7.94, 7.94) * mm, "end": v(8.7, 7.94) * mm});
            skLineSegment(sketch, "E117", {"start": v(9.52, 6.35) * mm, "end": v(10.29, 6.35) * mm});
            skLineSegment(sketch, "E118", {"start": v(11.11, 7.94) * mm, "end": v(11.87, 7.94) * mm});
            skLineSegment(sketch, "E119", {"start": v(12.7, 3.17) * mm, "end": v(13.46, 3.17) * mm});
            skLineSegment(sketch, "E120", {"start": v(14.29, 7.94) * mm, "end": v(15.05, 7.94) * mm});
            skLineSegment(sketch, "E121", {"start": v(15.87, 6.35) * mm, "end": v(16.64, 6.35) * mm});
            skLineSegment(sketch, "E122", {"start": v(17.46, 7.94) * mm, "end": v(18.22, 7.94) * mm});
            skLineSegment(sketch, "E123", {"start": v(19.05, 4.76) * mm, "end": v(19.81, 4.76) * mm});
            skLineSegment(sketch, "E124", {"start": v(20.64, 7.94) * mm, "end": v(21.4, 7.94) * mm});
            skLineSegment(sketch, "E125", {"start": v(22.22, 6.35) * mm, "end": v(22.99, 6.35) * mm});
            skLineSegment(sketch, "E126", {"start": v(23.81, 7.94) * mm, "end": v(24.57, 7.94) * mm});
            skLineSegment(sketch, "E127", {"start": v(25.4, 0) * mm, "end": v(26.16, 0) * mm});
            skLineSegment(sketch, "E128", {"start": v(26.99, 7.94) * mm, "end": v(27.75, 7.94) * mm});
            skLineSegment(sketch, "E129", {"start": v(28.57, 6.35) * mm, "end": v(29.34, 6.35) * mm});
            skLineSegment(sketch, "E130", {"start": v(30.16, 7.94) * mm, "end": v(30.92, 7.94) * mm});
            skLineSegment(sketch, "E131", {"start": v(31.75, 4.76) * mm, "end": v(32.51, 4.76) * mm});
            skLineSegment(sketch, "E132", {"start": v(33.34, 7.94) * mm, "end": v(34.1, 7.94) * mm});
            skLineSegment(sketch, "E133", {"start": v(34.92, 6.35) * mm, "end": v(35.69, 6.35) * mm});
            skLineSegment(sketch, "E134", {"start": v(36.51, 7.94) * mm, "end": v(37.27, 7.94) * mm});
            skLineSegment(sketch, "E135", {"start": v(38.1, 3.17) * mm, "end": v(38.86, 3.17) * mm});
            skLineSegment(sketch, "E136", {"start": v(39.69, 7.94) * mm, "end": v(40.45, 7.94) * mm});
            skLineSegment(sketch, "E137", {"start": v(41.27, 6.35) * mm, "end": v(42.04, 6.35) * mm});
            skLineSegment(sketch, "E138", {"start": v(42.86, 7.94) * mm, "end": v(43.62, 7.94) * mm});
            skLineSegment(sketch, "E139", {"start": v(44.45, 4.76) * mm, "end": v(45.21, 4.76) * mm});
            skLineSegment(sketch, "E140", {"start": v(46.04, 7.94) * mm, "end": v(46.8, 7.94) * mm});
            skLineSegment(sketch, "E141", {"start": v(47.62, 6.35) * mm, "end": v(48.39, 6.35) * mm});
            skLineSegment(sketch, "E142", {"start": v(49.21, 7.94) * mm, "end": v(49.97, 7.94) * mm});
            skLineSegment(sketch, "E143", {"start": v(50.8, 0) * mm, "end": v(51.56, 0) * mm});
            skLineSegment(sketch, "E144", {"start": v(52.39, 7.94) * mm, "end": v(53.15, 7.94) * mm});
            skLineSegment(sketch, "E145", {"start": v(53.97, 6.35) * mm, "end": v(54.74, 6.35) * mm});
            skLineSegment(sketch, "E146", {"start": v(55.56, 7.94) * mm, "end": v(56.32, 7.94) * mm});
            skLineSegment(sketch, "E147", {"start": v(57.15, 4.76) * mm, "end": v(57.91, 4.76) * mm});
            skLineSegment(sketch, "E148", {"start": v(58.74, 7.94) * mm, "end": v(59.5, 7.94) * mm});
            skLineSegment(sketch, "E149", {"start": v(60.32, 6.35) * mm, "end": v(61.09, 6.35) * mm});
            skLineSegment(sketch, "E150", {"start": v(61.91, 7.94) * mm, "end": v(62.67, 7.94) * mm});
            skLineSegment(sketch, "E151", {"start": v(63.5, 3.17) * mm, "end": v(64.26, 3.17) * mm});
            skLineSegment(sketch, "E152", {"start": v(65.09, 7.94) * mm, "end": v(65.85, 7.94) * mm});
            skLineSegment(sketch, "E153", {"start": v(66.67, 6.35) * mm, "end": v(67.44, 6.35) * mm});
            skLineSegment(sketch, "E154", {"start": v(68.26, 7.94) * mm, "end": v(69.02, 7.94) * mm});
            skLineSegment(sketch, "E155", {"start": v(69.85, 4.76) * mm, "end": v(70.61, 4.76) * mm});
            skLineSegment(sketch, "E156", {"start": v(71.44, 7.94) * mm, "end": v(72.2, 7.94) * mm});
            skLineSegment(sketch, "E157", {"start": v(73.02, 6.35) * mm, "end": v(73.79, 6.35) * mm});
            skLineSegment(sketch, "E158", {"start": v(74.61, 7.94) * mm, "end": v(75.37, 7.94) * mm});
            skSolve(sketch);
        }
        {
            var Q0;
            {var subQ133=sQuery(id+"F2.wireOp",EDGE,"E2.1.0.0");Q0=makeQuery(id+"F2.imprint","IMPRINT",FACE,{"disambiguationData":[TD([[makeQuery(id+"F2.imprint","IMPRINT",EDGE,{"derivedFrom":subQ133}),-1.0]])]});}
            var Q1;
            Q1=sQuery(id+"F2.wireOp",EDGE,"E10.5.0.0");
            var Q2;
            Q2=sQuery(id+"F2.wireOp",EDGE,"E67");
            var Q3;
            Q3=sQuery(id+"F2.wireOp",EDGE,"E52.5.0.0");
            var Q4;
            Q4=sQuery(id+"F2.wireOp",EDGE,"E6.1.0.0");
            var Q5;
            Q5=sQuery(id+"F2.wireOp",EDGE,"E69");
            var Q6;
            Q6=sQuery(id+"F2.wireOp",EDGE,"E54.1.0.0");
            var Q7;
            Q7=sQuery(id+"F2.wireOp",EDGE,"E3");
            var Q8;
            Q8=sQuery(id+"F2.wireOp",EDGE,"E49");
            var Q9;
            Q9=sQuery(id+"F2.wireOp",EDGE,"E8.2.0.0");
            var Q10;
            Q10=sQuery(id+"F2.wireOp",EDGE,"E53.2.0.0");
            var Q11;
            Q11=sQuery(id+"F2.wireOp",EDGE,"E38");
            var Q12;
            Q12=sQuery(id+"F2.wireOp",EDGE,"E9");
            var Q13;
            Q13=sQuery(id+"F2.wireOp",EDGE,"E39");
            var Q14;
            Q14=sQuery(id+"F2.wireOp",EDGE,"E7");
            var Q15;
            Q15=sQuery(id+"F2.wireOp",EDGE,"E41");
            var Q16;
            Q16=sQuery(id+"F2.wireOp",EDGE,"E42");
            var Q17;
            Q17=sQuery(id+"F2.wireOp",EDGE,"E10.1.0.0");
            var Q18;
            Q18=sQuery(id+"F2.wireOp",EDGE,"E52.1.0.0");
            var Q19;
            Q19=sQuery(id+"F2.wireOp",EDGE,"E56");
            var Q20;
            Q20=sQuery(id+"F2.wireOp",EDGE,"E5");
            var Q21;
            Q21=sQuery(id+"F2.wireOp",EDGE,"E46");
            var Q22;
            Q22=sQuery(id+"F2.wireOp",EDGE,"E48");
            var Q23;
            Q23=sQuery(id+"F2.wireOp",EDGE,"E10.2.0.0");
            var Q24;
            Q24=sQuery(id+"F2.wireOp",EDGE,"E52.2.0.0");
            var Q25;
            Q25=sQuery(id+"F2.wireOp",EDGE,"E55");
            var Q26;
            Q26=sQuery(id+"F2.wireOp",EDGE,"E8.1.0.0");
            var Q27;
            Q27=sQuery(id+"F2.wireOp",EDGE,"E53.1.0.0");
            var Q28;
            Q28=sQuery(id+"F2.wireOp",EDGE,"E61");
            var Q29;
            Q29=sQuery(id+"F2.wireOp",EDGE,"E10.3.0.0");
            var Q30;
            Q30=sQuery(id+"F2.wireOp",EDGE,"E58");
            var Q31;
            Q31=sQuery(id+"F2.wireOp",EDGE,"E52.3.0.0");
            var Q32;
            Q32=sQuery(id+"F2.wireOp",EDGE,"E10.4.0.0");
            var Q33;
            Q33=sQuery(id+"F2.wireOp",EDGE,"E52.4.0.0");
            var Q34;
            Q34=sQuery(id+"F2.wireOp",EDGE,"E63");
            var Q35;
            Q35=sQuery(id+"F2.wireOp",EDGE,"E10.6.0.0");
            var Q36;
            Q36=sQuery(id+"F2.wireOp",EDGE,"E52.6.0.0");
            var Q37;
            Q37=sQuery(id+"F2.wireOp",EDGE,"E70");
            var Q38;
            Q38=sQuery(id+"F2.wireOp",EDGE,"E8.3.0.0");
            var Q39;
            Q39=sQuery(id+"F2.wireOp",EDGE,"E53.3.0.0");
            var Q40;
            Q40=sQuery(id+"F2.wireOp",EDGE,"E73");
            var Q41;
            Q41=sQuery(id+"F2.wireOp",EDGE,"E52.7.0.0");
            var Q42;
            Q42=sQuery(id+"F2.wireOp",EDGE,"E74");
            var Q43;
            Q43=sQuery(id+"F2.wireOp",EDGE,"E10.7.0.0");
            var Q44;
            Q44=sQuery(id+"F2.wireOp",EDGE,"E1");
            var Q45;
            Q45=sQuery(id+"F2.wireOp",EDGE,"E79");
            var Q46;
            Q46=sQuery(id+"F2.wireOp",EDGE,"E77");
            var Q47;
            Q47=sQuery(id+"F2.wireOp",EDGE,"E10.8.0.0");
            var Q48;
            Q48=sQuery(id+"F2.wireOp",EDGE,"E75");
            var Q49;
            Q49=sQuery(id+"F2.wireOp",EDGE,"E52.8.0.0");
            var Q50;
            Q50=sQuery(id+"F2.wireOp",EDGE,"E8.4.0.0");
            var Q51;
            Q51=sQuery(id+"F2.wireOp",EDGE,"E81");
            var Q52;
            Q52=sQuery(id+"F2.wireOp",EDGE,"E53.4.0.0");
            var Q53;
            Q53=sQuery(id+"F2.wireOp",EDGE,"E10.9.0.0");
            var Q54;
            Q54=sQuery(id+"F2.wireOp",EDGE,"E82");
            var Q55;
            Q55=sQuery(id+"F2.wireOp",EDGE,"E52.9.0.0");
            var Q56;
            Q56=sQuery(id+"F2.wireOp",EDGE,"E6.2.0.0");
            var Q57;
            Q57=sQuery(id+"F2.wireOp",EDGE,"E83");
            var Q58;
            Q58=sQuery(id+"F2.wireOp",EDGE,"E54.2.0.0");
            var Q59;
            Q59=sQuery(id+"F2.wireOp",EDGE,"E10.10.0.0");
            var Q60;
            Q60=sQuery(id+"F2.wireOp",EDGE,"E84");
            var Q61;
            Q61=sQuery(id+"F2.wireOp",EDGE,"E52.10.0.0");
            var Q62;
            Q62=sQuery(id+"F2.wireOp",EDGE,"E8.5.0.0");
            var Q63;
            Q63=sQuery(id+"F2.wireOp",EDGE,"E85");
            var Q64;
            Q64=sQuery(id+"F2.wireOp",EDGE,"E53.5.0.0");
            var Q65;
            Q65=sQuery(id+"F2.wireOp",EDGE,"E10.11.0.0");
            var Q66;
            Q66=sQuery(id+"F2.wireOp",EDGE,"E86");
            var Q67;
            Q67=sQuery(id+"F2.wireOp",EDGE,"E52.11.0.0");
            var Q68;
            Q68=sQuery(id+"F2.wireOp",EDGE,"E76.1.0.0");
            var Q69;
            Q69=sQuery(id+"F2.wireOp",EDGE,"E4.1.0.0");
            var Q70;
            Q70=sQuery(id+"F2.wireOp",EDGE,"E87");
            var Q71;
            Q71=sQuery(id+"F2.wireOp",EDGE,"E10.12.0.0");
            var Q72;
            Q72=sQuery(id+"F2.wireOp",EDGE,"E52.12.0.0");
            var Q73;
            Q73=sQuery(id+"F2.wireOp",EDGE,"E88");
            var Q74;
            Q74=sQuery(id+"F2.wireOp",EDGE,"E8.6.0.0");
            var Q75;
            Q75=sQuery(id+"F2.wireOp",EDGE,"E53.6.0.0");
            var Q76;
            Q76=sQuery(id+"F2.wireOp",EDGE,"E89");
            var Q77;
            Q77=sQuery(id+"F2.wireOp",EDGE,"E10.13.0.0");
            var Q78;
            Q78=sQuery(id+"F2.wireOp",EDGE,"E52.13.0.0");
            var Q79;
            Q79=sQuery(id+"F2.wireOp",EDGE,"E90");
            var Q80;
            Q80=sQuery(id+"F2.wireOp",EDGE,"E6.3.0.0");
            var Q81;
            Q81=sQuery(id+"F2.wireOp",EDGE,"E54.3.0.0");
            var Q82;
            Q82=sQuery(id+"F2.wireOp",EDGE,"E91");
            var Q83;
            Q83=sQuery(id+"F2.wireOp",EDGE,"E10.14.0.0");
            var Q84;
            Q84=sQuery(id+"F2.wireOp",EDGE,"E52.14.0.0");
            var Q85;
            Q85=sQuery(id+"F2.wireOp",EDGE,"E92");
            var Q86;
            Q86=sQuery(id+"F2.wireOp",EDGE,"E53.7.0.0");
            var Q87;
            Q87=sQuery(id+"F2.wireOp",EDGE,"E8.7.0.0");
            var Q88;
            Q88=sQuery(id+"F2.wireOp",EDGE,"E93");
            var Q89;
            Q89=sQuery(id+"F2.wireOp",EDGE,"E10.15.0.0");
            var Q90;
            Q90=sQuery(id+"F2.wireOp",EDGE,"E94");
            var Q91;
            Q91=sQuery(id+"F2.wireOp",EDGE,"E52.15.0.0");
            var Q92;
            Q92=sQuery(id+"F2.wireOp",EDGE,"E2.1.0.0");
            var Q93;
            Q93=sQuery(id+"F2.wireOp",EDGE,"E95");
            var Q94;
            Q94=sQuery(id+"F2.wireOp",EDGE,"E80.1.0.0");
            var Q95;
            Q95=sQuery(id+"F2.wireOp",EDGE,"E10.16.0.0");
            var Q96;
            Q96=sQuery(id+"F2.wireOp",EDGE,"E96");
            var Q97;
            Q97=sQuery(id+"F2.wireOp",EDGE,"E52.16.0.0");
            var Q98;
            Q98=sQuery(id+"F2.wireOp",EDGE,"E8.8.0.0");
            var Q99;
            Q99=sQuery(id+"F2.wireOp",EDGE,"E53.8.0.0");
            var Q100;
            Q100=sQuery(id+"F2.wireOp",EDGE,"E97");
            var Q101;
            Q101=sQuery(id+"F2.wireOp",EDGE,"E10.17.0.0");
            var Q102;
            Q102=sQuery(id+"F2.wireOp",EDGE,"E52.17.0.0");
            var Q103;
            Q103=sQuery(id+"F2.wireOp",EDGE,"E98");
            var Q104;
            Q104=sQuery(id+"F2.wireOp",EDGE,"E54.4.0.0");
            var Q105;
            Q105=sQuery(id+"F2.wireOp",EDGE,"E6.4.0.0");
            var Q106;
            Q106=sQuery(id+"F2.wireOp",EDGE,"E99");
            var Q107;
            Q107=sQuery(id+"F2.wireOp",EDGE,"E10.18.0.0");
            var Q108;
            Q108=sQuery(id+"F2.wireOp",EDGE,"E107");
            var Q109;
            Q109=sQuery(id+"F2.wireOp",EDGE,"E105");
            var Q110;
            Q110=sQuery(id+"F2.wireOp",EDGE,"E101");
            var Q111;
            Q111=sQuery(id+"F2.wireOp",EDGE,"E11.0");
            var Q112;
            Q112=sQuery(id+"F2.wireOp",EDGE,"E80.4.0.0");
            var Q113;
            Q113=sQuery(id+"F2.wireOp",EDGE,"E80.2.0.0");
            var Q114;
            Q114=sQuery(id+"F2.wireOp",EDGE,"E11.1");
            var Q115;
            Q115=sQuery(id+"F2.wireOp",EDGE,"E11.2");
            var Q116;
            Q116=sQuery(id+"F2.wireOp",EDGE,"E80.3.0.0");
            var Q117;
            Q117=sQuery(id+"F2.wireOp",EDGE,"E4.2.0.0");
            var Q118;
            Q118=sQuery(id+"F2.wireOp",EDGE,"E4.5.0.0");
            var Q119;
            Q119=sQuery(id+"F2.wireOp",EDGE,"E2.3.0.0");
            var Q120;
            Q120=sQuery(id+"F2.wireOp",EDGE,"E2.2.0.0");
            var Q121;
            Q121=sQuery(id+"F2.wireOp",EDGE,"E4.4.0.0");
            var Q122;
            Q122=sQuery(id+"F2.wireOp",EDGE,"E2.4.0.0");
            var Q123;
            Q123=sQuery(id+"F2.wireOp",EDGE,"E4.3.0.0");
            var Q124;
            Q124=sQuery(id+"F2.wireOp",EDGE,"E1");
            var Q125;
            Q125=sQuery(id+"F2.wireOp",EDGE,"E76.3.0.0");
            var Q126;
            Q126=sQuery(id+"F2.wireOp",EDGE,"E76.2.0.0");
            var Q127;
            Q127=sQuery(id+"F2.wireOp",EDGE,"E27.MirrorCS");
            var Q128;
            Q128=sQuery(id+"F2.wireOp",EDGE,"E76.5.0.0");
            var Q129;
            Q129=sQuery(id+"F2.wireOp",EDGE,"E52.31.0.0");
            var Q130;
            Q130=sQuery(id+"F2.wireOp",EDGE,"E6.7.0.0");
            var Q131;
            Q131=sQuery(id+"F2.wireOp",EDGE,"E103");
            var Q132;
            Q132=sQuery(id+"F2.wireOp",EDGE,"E76.4.0.0");
            var Q133;
            Q133=sQuery(id+"F2.wireOp",EDGE,"E119");
            var Q134;
            Q134=sQuery(id+"F2.wireOp",EDGE,"E151");
            var Q135;
            Q135=sQuery(id+"F2.wireOp",EDGE,"E10.29.0.0");
            var Q136;
            Q136=sQuery(id+"F2.wireOp",EDGE,"E6.5.0.0");
            var Q137;
            Q137=sQuery(id+"F2.wireOp",EDGE,"E143");
            var Q138;
            Q138=sQuery(id+"F2.wireOp",EDGE,"E111");
            var Q139;
            Q139=sQuery(id+"F2.wireOp",EDGE,"E127");
            var Q140;
            Q140=sQuery(id+"F2.wireOp",EDGE,"E8.16.0.0");
            var Q141;
            Q141=sQuery(id+"F2.wireOp",EDGE,"E16.MirrorCS");
            var Q142;
            Q142=sQuery(id+"F2.wireOp",EDGE,"E53.12.0.0");
            var Q143;
            Q143=sQuery(id+"F2.wireOp",EDGE,"E10.22.0.0");
            var Q144;
            Q144=sQuery(id+"F2.wireOp",EDGE,"E53.11.0.0");
            var Q145;
            Q145=sQuery(id+"F2.wireOp",EDGE,"E10.25.0.0");
            var Q146;
            Q146=sQuery(id+"F2.wireOp",EDGE,"E129");
            var Q147;
            Q147=sQuery(id+"F2.wireOp",EDGE,"E10.32.0.0");
            var Q148;
            Q148=sQuery(id+"F2.wireOp",EDGE,"E135");
            var Q149;
            Q149=sQuery(id+"F2.wireOp",EDGE,"E52.47.0.0");
            var Q150;
            Q150=sQuery(id+"F2.wireOp",EDGE,"E10.30.0.0");
            var Q151;
            Q151=sQuery(id+"F2.wireOp",EDGE,"E8.10.0.0");
            var Q152;
            Q152=sQuery(id+"F2.wireOp",EDGE,"E53.20.0.0");
            var Q153;
            Q153=sQuery(id+"F2.wireOp",EDGE,"E53.21.0.0");
            var Q154;
            Q154=sQuery(id+"F2.wireOp",EDGE,"E52.36.0.0");
            var Q155;
            Q155=sQuery(id+"F2.wireOp",EDGE,"E10.33.0.0");
            var Q156;
            Q156=sQuery(id+"F2.wireOp",EDGE,"E123");
            var Q157;
            Q157=sQuery(id+"F2.wireOp",EDGE,"E124");
            var Q158;
            Q158=sQuery(id+"F2.wireOp",EDGE,"E54.6.0.0");
            var Q159;
            Q159=sQuery(id+"F2.wireOp",EDGE,"E52.32.0.0");
            var Q160;
            Q160=sQuery(id+"F2.wireOp",EDGE,"E6.6.0.0");
            var Q161;
            Q161=sQuery(id+"F2.wireOp",EDGE,"E10.31.0.0");
            var Q162;
            Q162=sQuery(id+"F2.wireOp",EDGE,"E51");
            var Q163;
            Q163=sQuery(id+"F2.wireOp",EDGE,"E10.26.0.0");
            var Q164;
            Q164=sQuery(id+"F2.wireOp",EDGE,"E52.29.0.0");
            var Q165;
            Q165=sQuery(id+"F2.wireOp",EDGE,"E53.14.0.0");
            var Q166;
            Q166=sQuery(id+"F2.wireOp",EDGE,"E10.28.0.0");
            var Q167;
            Q167=sQuery(id+"F2.wireOp",EDGE,"E52.18.0.0");
            var Q168;
            Q168=sQuery(id+"F2.wireOp",EDGE,"E54.5.0.0");
            var Q169;
            Q169=sQuery(id+"F2.wireOp",EDGE,"E54.7.0.0");
            var Q170;
            Q170=sQuery(id+"F2.wireOp",EDGE,"E10.20.0.0");
            var Q171;
            Q171=sQuery(id+"F2.wireOp",EDGE,"E8.13.0.0");
            var Q172;
            Q172=sQuery(id+"F2.wireOp",EDGE,"E8.14.0.0");
            var Q173;
            Q173=sQuery(id+"F2.wireOp",EDGE,"E10.21.0.0");
            var Q174;
            Q174=sQuery(id+"F2.wireOp",EDGE,"E10.19.0.0");
            var Q175;
            Q175=sQuery(id+"F2.wireOp",EDGE,"E52.22.0.0");
            var Q176;
            Q176=sQuery(id+"F2.wireOp",EDGE,"E52.23.0.0");
            var Q177;
            Q177=sQuery(id+"F2.wireOp",EDGE,"E8.12.0.0");
            var Q178;
            Q178=sQuery(id+"F2.wireOp",EDGE,"E52.39.0.0");
            var Q179;
            Q179=sQuery(id+"F2.wireOp",EDGE,"E26.MirrorCS");
            var Q180;
            Q180=sQuery(id+"F2.wireOp",EDGE,"E8.11.0.0");
            var Q181;
            Q181=sQuery(id+"F2.wireOp",EDGE,"E10.24.0.0");
            var Q182;
            Q182=sQuery(id+"F2.wireOp",EDGE,"E113");
            var Q183;
            Q183=sQuery(id+"F2.wireOp",EDGE,"E13.MirrorCS");
            var Q184;
            Q184=sQuery(id+"F2.wireOp",EDGE,"E52.25.0.0");
            var Q185;
            Q185=sQuery(id+"F2.wireOp",EDGE,"E145");
            var Q186;
            Q186=sQuery(id+"F2.wireOp",EDGE,"E8.18.0.0");
            var Q187;
            Q187=sQuery(id+"F2.wireOp",EDGE,"E52.28.0.0");
            var Q188;
            Q188=sQuery(id+"F2.wireOp",EDGE,"E52.26.0.0");
            var Q189;
            Q189=sQuery(id+"F2.wireOp",EDGE,"E52.43.0.0");
            var Q190;
            Q190=sQuery(id+"F2.wireOp",EDGE,"E8.15.0.0");
            var Q191;
            Q191=sQuery(id+"F2.wireOp",EDGE,"E53.10.0.0");
            var Q192;
            Q192=sQuery(id+"F2.wireOp",EDGE,"E53.9.0.0");
            var Q193;
            Q193=sQuery(id+"F2.wireOp",EDGE,"E10.23.0.0");
            var Q194;
            Q194=sQuery(id+"F2.wireOp",EDGE,"E52.42.0.0");
            var Q195;
            Q195=sQuery(id+"F2.wireOp",EDGE,"E52.27.0.0");
            var Q196;
            Q196=sQuery(id+"F2.wireOp",EDGE,"E128");
            var Q197;
            Q197=sQuery(id+"F2.wireOp",EDGE,"E6.11.0.0");
            var Q198;
            Q198=sQuery(id+"F2.wireOp",EDGE,"E31.MirrorCS");
            var Q199;
            Q199=sQuery(id+"F2.wireOp",EDGE,"E53.16.0.0");
            var Q200;
            Q200=sQuery(id+"F2.wireOp",EDGE,"E52.20.0.0");
            var Q201;
            Q201=sQuery(id+"F2.wireOp",EDGE,"E53.18.0.0");
            var Q202;
            Q202=sQuery(id+"F2.wireOp",EDGE,"E22.MirrorCS");
            var Q203;
            Q203=sQuery(id+"F2.wireOp",EDGE,"E150");
            var Q204;
            Q204=sQuery(id+"F2.wireOp",EDGE,"E10.27.0.0");
            var Q205;
            Q205=sQuery(id+"F2.wireOp",EDGE,"E120");
            var Q206;
            Q206=sQuery(id+"F2.wireOp",EDGE,"E54.8.0.0");
            var Q207;
            Q207=sQuery(id+"F2.wireOp",EDGE,"E108");
            var Q208;
            Q208=sQuery(id+"F2.wireOp",EDGE,"E155");
            var Q209;
            Q209=sQuery(id+"F2.wireOp",EDGE,"E40");
            var Q210;
            Q210=sQuery(id+"F2.wireOp",EDGE,"E54.11.0.0");
            var Q211;
            Q211=sQuery(id+"F2.wireOp",EDGE,"E52.19.0.0");
            var Q212;
            Q212=sQuery(id+"F2.wireOp",EDGE,"E53.13.0.0");
            var Q213;
            Q213=sQuery(id+"F2.wireOp",EDGE,"E53.19.0.0");
            var Q214;
            Q214=sQuery(id+"F2.wireOp",EDGE,"E52.30.0.0");
            var Q215;
            Q215=sQuery(id+"F2.wireOp",EDGE,"E8.9.0.0");
            var Q216;
            Q216=sQuery(id+"F2.wireOp",EDGE,"E53.15.0.0");
            var Q217;
            Q217=sQuery(id+"F2.wireOp",EDGE,"E122");
            var Q218;
            Q218=sQuery(id+"F2.wireOp",EDGE,"E52.34.0.0");
            var Q219;
            Q219=sQuery(id+"F2.wireOp",EDGE,"E118");
            var Q220;
            Q220=sQuery(id+"F2.wireOp",EDGE,"E117");
            var Q221;
            Q221=sQuery(id+"F2.wireOp",EDGE,"E36.MirrorCS");
            var Q222;
            Q222=sQuery(id+"F2.wireOp",EDGE,"E100");
            var Q223;
            Q223=sQuery(id+"F2.wireOp",EDGE,"E8.21.0.0");
            var Q224;
            Q224=sQuery(id+"F2.wireOp",EDGE,"E116");
            var Q225;
            Q225=sQuery(id+"F2.wireOp",EDGE,"E10.46.0.0");
            var Q226;
            Q226=sQuery(id+"F2.wireOp",EDGE,"E104");
            var Q227;
            Q227=sQuery(id+"F2.wireOp",EDGE,"E21.MirrorCS");
            var Q228;
            Q228=sQuery(id+"F2.wireOp",EDGE,"E121");
            var Q229;
            Q229=sQuery(id+"F2.wireOp",EDGE,"E52.24.0.0");
            var Q230;
            Q230=sQuery(id+"F2.wireOp",EDGE,"E78");
            var Q231;
            Q231=sQuery(id+"F2.wireOp",EDGE,"E68");
            var Q232;
            Q232=sQuery(id+"F2.wireOp",EDGE,"E12.MirrorCS");
            var Q233;
            Q233=sQuery(id+"F2.wireOp",EDGE,"E109");
            var Q234;
            Q234=sQuery(id+"F2.wireOp",EDGE,"E125");
            var Q235;
            Q235=sQuery(id+"F2.wireOp",EDGE,"E53.23.0.0");
            var Q236;
            Q236=sQuery(id+"F2.wireOp",EDGE,"E6.9.0.0");
            var Q237;
            Q237=sQuery(id+"F2.wireOp",EDGE,"E126");
            var Q238;
            Q238=sQuery(id+"F2.wireOp",EDGE,"E72");
            var Q239;
            Q239=sQuery(id+"F2.wireOp",EDGE,"E110");
            var Q240;
            Q240=sQuery(id+"F2.wireOp",EDGE,"E10.35.0.0");
            var Q241;
            Q241=sQuery(id+"F2.wireOp",EDGE,"E53.22.0.0");
            var Q242;
            Q242=sQuery(id+"F2.wireOp",EDGE,"E52.21.0.0");
            var Q243;
            Q243=sQuery(id+"F2.wireOp",EDGE,"E10.34.0.0");
            var Q244;
            Q244=sQuery(id+"F2.wireOp",EDGE,"E6.8.0.0");
            var Q245;
            Q245=sQuery(id+"F2.wireOp",EDGE,"E29.MirrorCS");
            var Q246;
            Q246=sQuery(id+"F2.wireOp",EDGE,"E114");
            var Q247;
            Q247=sQuery(id+"F2.wireOp",EDGE,"E52.44.0.0");
            var Q248;
            Q248=sQuery(id+"F2.wireOp",EDGE,"E10.40.0.0");
            var Q249;
            Q249=sQuery(id+"F2.wireOp",EDGE,"E8.17.0.0");
            var Q250;
            Q250=sQuery(id+"F2.wireOp",EDGE,"E112");
            var Q251;
            Q251=sQuery(id+"F2.wireOp",EDGE,"E15.MirrorCS");
            var Q252;
            Q252=sQuery(id+"F2.wireOp",EDGE,"E32.MirrorCS");
            var Q253;
            Q253=sQuery(id+"F2.wireOp",EDGE,"E10.39.0.0");
            var Q254;
            Q254=sQuery(id+"F2.wireOp",EDGE,"E30.MirrorCS");
            var Q255;
            Q255=sQuery(id+"F2.wireOp",EDGE,"E115");
            var Q256;
            Q256=sQuery(id+"F2.wireOp",EDGE,"E14.MirrorCS");
            var Q257;
            Q257=sQuery(id+"F2.wireOp",EDGE,"E10.41.0.0");
            var Q258;
            Q258=sQuery(id+"F2.wireOp",EDGE,"E28.MirrorCS");
            var Q259;
            Q259=sQuery(id+"F2.wireOp",EDGE,"E156");
            var Q260;
            Q260=sQuery(id+"F2.wireOp",EDGE,"E10.43.0.0");
            var Q261;
            Q261=sQuery(id+"F2.wireOp",EDGE,"E106");
            var Q262;
            Q262=sQuery(id+"F2.wireOp",EDGE,"E8.23.0.0");
            var Q263;
            Q263=sQuery(id+"F2.wireOp",EDGE,"E54.9.0.0");
            var Q264;
            Q264=sQuery(id+"F2.wireOp",EDGE,"E10.45.0.0");
            var Q265;
            Q265=sQuery(id+"F2.wireOp",EDGE,"E8.20.0.0");
            var Q266;
            Q266=sQuery(id+"F2.wireOp",EDGE,"E149");
            var Q267;
            Q267=sQuery(id+"F2.wireOp",EDGE,"E8.22.0.0");
            var Q268;
            Q268=sQuery(id+"F2.wireOp",EDGE,"E148");
            var Q269;
            Q269=sQuery(id+"F2.wireOp",EDGE,"E52.35.0.0");
            var Q270;
            Q270=sQuery(id+"F2.wireOp",EDGE,"E24.MirrorCS");
            var Q271;
            Q271=sQuery(id+"F2.wireOp",EDGE,"E64");
            var Q272;
            Q272=sQuery(id+"F2.wireOp",EDGE,"E20.MirrorCS");
            var Q273;
            Q273=sQuery(id+"F2.wireOp",EDGE,"E152");
            var Q274;
            Q274=sQuery(id+"F2.wireOp",EDGE,"E153");
            var Q275;
            Q275=sQuery(id+"F2.wireOp",EDGE,"E10.47.0.0");
            var Q276;
            Q276=sQuery(id+"F2.wireOp",EDGE,"E132");
            var Q277;
            Q277=sQuery(id+"F2.wireOp",EDGE,"E154");
            var Q278;
            Q278=sQuery(id+"F2.wireOp",EDGE,"E33.MirrorCS");
            var Q279;
            Q279=sQuery(id+"F2.wireOp",EDGE,"E136");
            var Q280;
            Q280=sQuery(id+"F2.wireOp",EDGE,"E137");
            var Q281;
            Q281=sQuery(id+"F2.wireOp",EDGE,"E17.MirrorCS");
            var Q282;
            Q282=sQuery(id+"F2.wireOp",EDGE,"E10.44.0.0");
            var Q283;
            Q283=sQuery(id+"F2.wireOp",EDGE,"E54.10.0.0");
            var Q284;
            Q284=sQuery(id+"F2.wireOp",EDGE,"E50");
            var Q285;
            Q285=sQuery(id+"F2.wireOp",EDGE,"E34.MirrorCS");
            var Q286;
            Q286=sQuery(id+"F2.wireOp",EDGE,"E52.40.0.0");
            var Q287;
            Q287=sQuery(id+"F2.wireOp",EDGE,"E6.10.0.0");
            var Q288;
            Q288=sQuery(id+"F2.wireOp",EDGE,"E43");
            var Q289;
            Q289=sQuery(id+"F2.wireOp",EDGE,"E10.36.0.0");
            var Q290;
            Q290=sQuery(id+"F2.wireOp",EDGE,"E141");
            var Q291;
            Q291=sQuery(id+"F2.wireOp",EDGE,"E71");
            var Q292;
            Q292=sQuery(id+"F2.wireOp",EDGE,"E157");
            var Q293;
            Q293=sQuery(id+"F2.wireOp",EDGE,"E142");
            var Q294;
            Q294=sQuery(id+"F2.wireOp",EDGE,"E158");
            var Q295;
            Q295=sQuery(id+"F2.wireOp",EDGE,"E45");
            var Q296;
            Q296=sQuery(id+"F2.wireOp",EDGE,"E102");
            var Q297;
            Q297=sQuery(id+"F2.wireOp",EDGE,"E52.46.0.0");
            var Q298;
            Q298=sQuery(id+"F2.wireOp",EDGE,"E47");
            var Q299;
            Q299=sQuery(id+"F2.wireOp",EDGE,"E130");
            var Q300;
            Q300=sQuery(id+"F2.wireOp",EDGE,"E10.38.0.0");
            var Q301;
            Q301=sQuery(id+"F2.wireOp",EDGE,"E52.41.0.0");
            var Q302;
            Q302=sQuery(id+"F2.wireOp",EDGE,"E60");
            var Q303;
            Q303=sQuery(id+"F2.wireOp",EDGE,"E131");
            var Q304;
            Q304=sQuery(id+"F2.wireOp",EDGE,"E147");
            var Q305;
            Q305=sQuery(id+"F2.wireOp",EDGE,"E59");
            var Q306;
            Q306=sQuery(id+"F2.wireOp",EDGE,"E144");
            var Q307;
            Q307=sQuery(id+"F2.wireOp",EDGE,"E10.37.0.0");
            var Q308;
            Q308=sQuery(id+"F2.wireOp",EDGE,"E139");
            var Q309;
            Q309=sQuery(id+"F2.wireOp",EDGE,"E25.MirrorCS");
            var Q310;
            Q310=sQuery(id+"F2.wireOp",EDGE,"E23.MirrorCS");
            var Q311;
            Q311=sQuery(id+"F2.wireOp",EDGE,"E65");
            var Q312;
            Q312=sQuery(id+"F2.wireOp",EDGE,"E52.33.0.0");
            var Q313;
            Q313=sQuery(id+"F2.wireOp",EDGE,"E18.MirrorCS");
            var Q314;
            Q314=sQuery(id+"F2.wireOp",EDGE,"E53.17.0.0");
            var Q315;
            Q315=sQuery(id+"F2.wireOp",EDGE,"E62");
            var Q316;
            Q316=sQuery(id+"F2.wireOp",EDGE,"E10.42.0.0");
            var Q317;
            Q317=sQuery(id+"F2.wireOp",EDGE,"E37.MirrorCS");
            var Q318;
            Q318=sQuery(id+"F2.wireOp",EDGE,"E19.MirrorCS");
            var Q319;
            Q319=sQuery(id+"F2.wireOp",EDGE,"E134");
            var Q320;
            Q320=sQuery(id+"F2.wireOp",EDGE,"E8.19.0.0");
            var Q321;
            Q321=sQuery(id+"F2.wireOp",EDGE,"E52.45.0.0");
            var Q322;
            Q322=sQuery(id+"F2.wireOp",EDGE,"E57");
            var Q323;
            Q323=sQuery(id+"F2.wireOp",EDGE,"E52.38.0.0");
            var Q324;
            Q324=sQuery(id+"F2.wireOp",EDGE,"E146");
            var Q325;
            Q325=sQuery(id+"F2.wireOp",EDGE,"E35.MirrorCS");
            var Q326;
            Q326=sQuery(id+"F2.wireOp",EDGE,"E52.37.0.0");
            var Q327;
            Q327=sQuery(id+"F2.wireOp",EDGE,"E18.MirrorCS");
            var Q328;
            Q328=sQuery(id+"F2.wireOp",EDGE,"E44");
            var Q329;
            Q329=sQuery(id+"F2.wireOp",EDGE,"E133");
            var Q330;
            Q330=sQuery(id+"F2.wireOp",EDGE,"E66");
            var Q331;
            Q331=sQuery(id+"F2.wireOp",EDGE,"E138");
            var Q332;
            Q332=sQuery(id+"F2.wireOp",EDGE,"E140");
            var Q333;
            Q333=sQuery(id+"F2.wireOp",EDGE,"E44");
            extrude(context, id + "F3", {"entities" : qUnion([Q0]), "operationType" : NewBodyOperationType.ADD, "surfaceEntities" : qUnion([Q1, Q2, Q3, Q4, Q5, Q6, Q7, Q8, Q9, Q10, Q11, Q12, Q13, Q14, Q15, Q16, Q17, Q18, Q19, Q20, Q21, Q22, Q23, Q24, Q25, Q26, Q27, Q28, Q29, Q30, Q31, Q32, Q33, Q34, Q35, Q36, Q37, Q38, Q39, Q40, Q41, Q42, Q43, Q44, Q45, Q46, Q47, Q48, Q49, Q50, Q51, Q52, Q53, Q54, Q55, Q56, Q57, Q58, Q59, Q60, Q61, Q62, Q63, Q64, Q65, Q66, Q67, Q68, Q69, Q70, Q71, Q72, Q73, Q74, Q75, Q76, Q77, Q78, Q79, Q80, Q81, Q82, Q83, Q84, Q85, Q86, Q87, Q88, Q89, Q90, Q91, Q92, Q93, Q94, Q95, Q96, Q97, Q98, Q99, Q100, Q101, Q102, Q103, Q104, Q105, Q106, Q107, Q108, Q109, Q110, Q111, Q112, Q113, Q114, Q115, Q116, Q117, Q118, Q119, Q120, Q121, Q122, Q123, Q124, Q125, Q126, Q127, Q128, Q129, Q130, Q131, Q132, Q133, Q134, Q135, Q136, Q137, Q138, Q139, Q140, Q141, Q142, Q143, Q144, Q145, Q146, Q147, Q148, Q149, Q150, Q151, Q152, Q153, Q154, Q155, Q156, Q157, Q158, Q159, Q160, Q161, Q162, Q163, Q164, Q165, Q166, Q167, Q168, Q169, Q170, Q171, Q172, Q173, Q174, Q175, Q176, Q177, Q178, Q179, Q180, Q181, Q182, Q183, Q184, Q185, Q186, Q187, Q188, Q189, Q190, Q191, Q192, Q193, Q194, Q195, Q196, Q197, Q198, Q199, Q200, Q201, Q202, Q203, Q204, Q205, Q206, Q207, Q208, Q209, Q210, Q211, Q212, Q213, Q214, Q215, Q216, Q217, Q218, Q219, Q220, Q221, Q222, Q223, Q224, Q225, Q226, Q227, Q228, Q229, Q230, Q231, Q232, Q233, Q234, Q235, Q236, Q237, Q238, Q239, Q240, Q241, Q242, Q243, Q244, Q245, Q246, Q247, Q248, Q249, Q250, Q251, Q252, Q253, Q254, Q255, Q256, Q257, Q258, Q259, Q260, Q261, Q262, Q263, Q264, Q265, Q266, Q267, Q268, Q269, Q270, Q271, Q272, Q273, Q274, Q275, Q276, Q277, Q278, Q279, Q280, Q281, Q282, Q283, Q284, Q285, Q286, Q287, Q288, Q289, Q290, Q291, Q292, Q293, Q294, Q295, Q296, Q297, Q298, Q299, Q300, Q301, Q302, Q303, Q304, Q305, Q306, Q307, Q308, Q309, Q310, Q311, Q312, Q313, Q314, Q315, Q316, Q317, Q318, Q319, Q320, Q321, Q322, Q323, Q324, Q325, Q326, Q327, Q328, Q329, Q330, Q331, Q332, Q333]), "depth" : 0.8 * mm});
        }
        {
            var Q0;
            Q0=makeQuery(id+"F3.opExtrude","CAP_FACE",FACE,{"disambiguationData":[OSD([sQuery(id+"F0.wireOp",EDGE,"E0.bottom"),sQuery(id+"F0.wireOp",EDGE,"E0.top"),sQuery(id+"F0.wireOp",EDGE,"E0.left"),sQuery(id+"F0.wireOp",EDGE,"E0.right"),sQuery(id+"F2.wireOp",EDGE,"E2.1.0.0"),sQuery(id+"F2.wireOp",EDGE,"E2.2.0.0"),sQuery(id+"F2.wireOp",EDGE,"E2.3.0.0"),sQuery(id+"F2.wireOp",EDGE,"E2.4.0.0"),sQuery(id+"F2.wireOp",EDGE,"E3"),sQuery(id+"F2.wireOp",EDGE,"E4.1.0.0"),sQuery(id+"F2.wireOp",EDGE,"E4.2.0.0"),sQuery(id+"F2.wireOp",EDGE,"E4.3.0.0"),sQuery(id+"F2.wireOp",EDGE,"E4.5.0.0"),sQuery(id+"F2.wireOp",EDGE,"E5"),sQuery(id+"F2.wireOp",EDGE,"E6.1.0.0"),sQuery(id+"F2.wireOp",EDGE,"E6.2.0.0"),sQuery(id+"F2.wireOp",EDGE,"E6.3.0.0"),sQuery(id+"F2.wireOp",EDGE,"E6.4.0.0"),sQuery(id+"F2.wireOp",EDGE,"E6.5.0.0"),sQuery(id+"F2.wireOp",EDGE,"E6.6.0.0"),sQuery(id+"F2.wireOp",EDGE,"E6.7.0.0"),sQuery(id+"F2.wireOp",EDGE,"E7"),sQuery(id+"F2.wireOp",EDGE,"E8.1.0.0"),sQuery(id+"F2.wireOp",EDGE,"E8.2.0.0"),sQuery(id+"F2.wireOp",EDGE,"E8.3.0.0"),sQuery(id+"F2.wireOp",EDGE,"E8.4.0.0"),sQuery(id+"F2.wireOp",EDGE,"E8.5.0.0"),sQuery(id+"F2.wireOp",EDGE,"E8.6.0.0"),sQuery(id+"F2.wireOp",EDGE,"E8.7.0.0"),sQuery(id+"F2.wireOp",EDGE,"E8.8.0.0"),sQuery(id+"F2.wireOp",EDGE,"E8.9.0.0"),sQuery(id+"F2.wireOp",EDGE,"E8.10.0.0"),sQuery(id+"F2.wireOp",EDGE,"E8.11.0.0"),sQuery(id+"F2.wireOp",EDGE,"E8.12.0.0"),sQuery(id+"F2.wireOp",EDGE,"E8.13.0.0"),sQuery(id+"F2.wireOp",EDGE,"E8.14.0.0"),sQuery(id+"F2.wireOp",EDGE,"E8.15.0.0"),sQuery(id+"F2.wireOp",EDGE,"E8.16.0.0"),sQuery(id+"F2.wireOp",EDGE,"E8.21.0.0"),sQuery(id+"F2.wireOp",EDGE,"E9"),sQuery(id+"F2.wireOp",EDGE,"E10.1.0.0"),sQuery(id+"F2.wireOp",EDGE,"E10.2.0.0"),sQuery(id+"F2.wireOp",EDGE,"E10.3.0.0"),sQuery(id+"F2.wireOp",EDGE,"E10.4.0.0"),sQuery(id+"F2.wireOp",EDGE,"E10.5.0.0"),sQuery(id+"F2.wireOp",EDGE,"E10.6.0.0"),sQuery(id+"F2.wireOp",EDGE,"E10.7.0.0"),sQuery(id+"F2.wireOp",EDGE,"E10.8.0.0"),sQuery(id+"F2.wireOp",EDGE,"E10.9.0.0"),sQuery(id+"F2.wireOp",EDGE,"E10.10.0.0"),sQuery(id+"F2.wireOp",EDGE,"E10.11.0.0"),sQuery(id+"F2.wireOp",EDGE,"E10.12.0.0"),sQuery(id+"F2.wireOp",EDGE,"E10.13.0.0"),sQuery(id+"F2.wireOp",EDGE,"E10.14.0.0"),sQuery(id+"F2.wireOp",EDGE,"E10.15.0.0"),sQuery(id+"F2.wireOp",EDGE,"E10.16.0.0"),sQuery(id+"F2.wireOp",EDGE,"E10.17.0.0"),sQuery(id+"F2.wireOp",EDGE,"E10.18.0.0"),sQuery(id+"F2.wireOp",EDGE,"E10.19.0.0"),sQuery(id+"F2.wireOp",EDGE,"E10.20.0.0"),sQuery(id+"F2.wireOp",EDGE,"E10.21.0.0"),sQuery(id+"F2.wireOp",EDGE,"E10.22.0.0"),sQuery(id+"F2.wireOp",EDGE,"E10.23.0.0"),sQuery(id+"F2.wireOp",EDGE,"E10.24.0.0"),sQuery(id+"F2.wireOp",EDGE,"E10.25.0.0"),sQuery(id+"F2.wireOp",EDGE,"E10.26.0.0"),sQuery(id+"F2.wireOp",EDGE,"E10.27.0.0"),sQuery(id+"F2.wireOp",EDGE,"E10.28.0.0"),sQuery(id+"F2.wireOp",EDGE,"E10.29.0.0"),sQuery(id+"F2.wireOp",EDGE,"E10.30.0.0"),sQuery(id+"F2.wireOp",EDGE,"E10.31.0.0"),sQuery(id+"F2.wireOp",EDGE,"E10.32.0.0"),sQuery(id+"F2.wireOp",EDGE,"E12.MirrorCS"),sQuery(id+"F2.wireOp",EDGE,"E13.MirrorCS"),sQuery(id+"F2.wireOp",EDGE,"E14.MirrorCS"),sQuery(id+"F2.wireOp",EDGE,"E15.MirrorCS"),sQuery(id+"F2.wireOp",EDGE,"E16.MirrorCS"),sQuery(id+"F2.wireOp",EDGE,"E17.MirrorCS"),sQuery(id+"F2.wireOp",EDGE,"E19.MirrorCS"),sQuery(id+"F2.wireOp",EDGE,"E20.MirrorCS"),sQuery(id+"F2.wireOp",EDGE,"E21.MirrorCS"),sQuery(id+"F2.wireOp",EDGE,"E22.MirrorCS"),sQuery(id+"F2.wireOp",EDGE,"E23.MirrorCS"),sQuery(id+"F2.wireOp",EDGE,"E24.MirrorCS"),sQuery(id+"F2.wireOp",EDGE,"E25.MirrorCS"),sQuery(id+"F2.wireOp",EDGE,"E26.MirrorCS"),sQuery(id+"F2.wireOp",EDGE,"E27.MirrorCS"),sQuery(id+"F2.wireOp",EDGE,"E28.MirrorCS"),sQuery(id+"F2.wireOp",EDGE,"E29.MirrorCS"),sQuery(id+"F2.wireOp",EDGE,"E30.MirrorCS"),sQuery(id+"F2.wireOp",EDGE,"E31.MirrorCS"),sQuery(id+"F2.wireOp",EDGE,"E32.MirrorCS"),sQuery(id+"F2.wireOp",EDGE,"E33.MirrorCS"),sQuery(id+"F2.wireOp",EDGE,"E34.MirrorCS"),sQuery(id+"F2.wireOp",EDGE,"E35.MirrorCS"),sQuery(id+"F2.wireOp",EDGE,"E36.MirrorCS"),sQuery(id+"F2.wireOp",EDGE,"E18.MirrorCS"),sQuery(id+"F2.wireOp",EDGE,"E37.MirrorCS"),sQuery(id+"F2.wireOp",EDGE,"E38"),sQuery(id+"F2.wireOp",EDGE,"E39"),sQuery(id+"F2.wireOp",EDGE,"E41"),sQuery(id+"F2.wireOp",EDGE,"E42"),sQuery(id+"F2.wireOp",EDGE,"E46"),sQuery(id+"F2.wireOp",EDGE,"E48"),sQuery(id+"F2.wireOp",EDGE,"E49"),sQuery(id+"F2.wireOp",EDGE,"E51"),sQuery(id+"F2.wireOp",EDGE,"E52.1.0.0"),sQuery(id+"F2.wireOp",EDGE,"E52.2.0.0"),sQuery(id+"F2.wireOp",EDGE,"E52.3.0.0"),sQuery(id+"F2.wireOp",EDGE,"E52.4.0.0"),sQuery(id+"F2.wireOp",EDGE,"E52.5.0.0"),sQuery(id+"F2.wireOp",EDGE,"E52.6.0.0"),sQuery(id+"F2.wireOp",EDGE,"E52.7.0.0"),sQuery(id+"F2.wireOp",EDGE,"E52.8.0.0"),sQuery(id+"F2.wireOp",EDGE,"E52.9.0.0"),sQuery(id+"F2.wireOp",EDGE,"E52.10.0.0"),sQuery(id+"F2.wireOp",EDGE,"E52.11.0.0"),sQuery(id+"F2.wireOp",EDGE,"E52.12.0.0"),sQuery(id+"F2.wireOp",EDGE,"E52.13.0.0"),sQuery(id+"F2.wireOp",EDGE,"E52.14.0.0"),sQuery(id+"F2.wireOp",EDGE,"E52.15.0.0"),sQuery(id+"F2.wireOp",EDGE,"E52.16.0.0"),sQuery(id+"F2.wireOp",EDGE,"E52.17.0.0"),sQuery(id+"F2.wireOp",EDGE,"E52.18.0.0"),sQuery(id+"F2.wireOp",EDGE,"E52.19.0.0"),sQuery(id+"F2.wireOp",EDGE,"E52.20.0.0"),sQuery(id+"F2.wireOp",EDGE,"E52.21.0.0"),sQuery(id+"F2.wireOp",EDGE,"E52.22.0.0"),sQuery(id+"F2.wireOp",EDGE,"E52.23.0.0"),sQuery(id+"F2.wireOp",EDGE,"E52.24.0.0"),sQuery(id+"F2.wireOp",EDGE,"E52.25.0.0"),sQuery(id+"F2.wireOp",EDGE,"E52.26.0.0"),sQuery(id+"F2.wireOp",EDGE,"E52.27.0.0"),sQuery(id+"F2.wireOp",EDGE,"E52.28.0.0"),sQuery(id+"F2.wireOp",EDGE,"E52.29.0.0"),sQuery(id+"F2.wireOp",EDGE,"E52.30.0.0"),sQuery(id+"F2.wireOp",EDGE,"E52.31.0.0"),sQuery(id+"F2.wireOp",EDGE,"E52.32.0.0"),sQuery(id+"F2.wireOp",EDGE,"E52.33.0.0"),sQuery(id+"F2.wireOp",EDGE,"E52.34.0.0"),sQuery(id+"F2.wireOp",EDGE,"E52.35.0.0"),sQuery(id+"F2.wireOp",EDGE,"E52.36.0.0"),sQuery(id+"F2.wireOp",EDGE,"E52.37.0.0"),sQuery(id+"F2.wireOp",EDGE,"E52.38.0.0"),sQuery(id+"F2.wireOp",EDGE,"E52.39.0.0"),sQuery(id+"F2.wireOp",EDGE,"E52.40.0.0"),sQuery(id+"F2.wireOp",EDGE,"E52.41.0.0"),sQuery(id+"F2.wireOp",EDGE,"E52.42.0.0"),sQuery(id+"F2.wireOp",EDGE,"E52.43.0.0"),sQuery(id+"F2.wireOp",EDGE,"E52.44.0.0"),sQuery(id+"F2.wireOp",EDGE,"E52.45.0.0"),sQuery(id+"F2.wireOp",EDGE,"E52.46.0.0"),sQuery(id+"F2.wireOp",EDGE,"E52.47.0.0"),sQuery(id+"F2.wireOp",EDGE,"E53.1.0.0"),sQuery(id+"F2.wireOp",EDGE,"E53.2.0.0"),sQuery(id+"F2.wireOp",EDGE,"E53.3.0.0"),sQuery(id+"F2.wireOp",EDGE,"E53.4.0.0"),sQuery(id+"F2.wireOp",EDGE,"E53.5.0.0"),sQuery(id+"F2.wireOp",EDGE,"E53.6.0.0"),sQuery(id+"F2.wireOp",EDGE,"E53.7.0.0"),sQuery(id+"F2.wireOp",EDGE,"E53.8.0.0"),sQuery(id+"F2.wireOp",EDGE,"E53.9.0.0"),sQuery(id+"F2.wireOp",EDGE,"E53.10.0.0"),sQuery(id+"F2.wireOp",EDGE,"E53.11.0.0"),sQuery(id+"F2.wireOp",EDGE,"E53.12.0.0"),sQuery(id+"F2.wireOp",EDGE,"E53.13.0.0"),sQuery(id+"F2.wireOp",EDGE,"E53.14.0.0"),sQuery(id+"F2.wireOp",EDGE,"E53.15.0.0"),sQuery(id+"F2.wireOp",EDGE,"E53.16.0.0"),sQuery(id+"F2.wireOp",EDGE,"E53.17.0.0"),sQuery(id+"F2.wireOp",EDGE,"E53.18.0.0"),sQuery(id+"F2.wireOp",EDGE,"E53.19.0.0"),sQuery(id+"F2.wireOp",EDGE,"E53.20.0.0"),sQuery(id+"F2.wireOp",EDGE,"E53.21.0.0"),sQuery(id+"F2.wireOp",EDGE,"E53.22.0.0"),sQuery(id+"F2.wireOp",EDGE,"E53.23.0.0"),sQuery(id+"F2.wireOp",EDGE,"E54.1.0.0"),sQuery(id+"F2.wireOp",EDGE,"E54.2.0.0"),sQuery(id+"F2.wireOp",EDGE,"E54.3.0.0"),sQuery(id+"F2.wireOp",EDGE,"E54.4.0.0"),sQuery(id+"F2.wireOp",EDGE,"E54.5.0.0"),sQuery(id+"F2.wireOp",EDGE,"E54.6.0.0"),sQuery(id+"F2.wireOp",EDGE,"E54.7.0.0"),sQuery(id+"F2.wireOp",EDGE,"E54.8.0.0"),sQuery(id+"F2.wireOp",EDGE,"E54.9.0.0"),sQuery(id+"F2.wireOp",EDGE,"E54.10.0.0"),sQuery(id+"F2.wireOp",EDGE,"E54.11.0.0"),sQuery(id+"F2.wireOp",EDGE,"E55"),sQuery(id+"F2.wireOp",EDGE,"E56"),sQuery(id+"F2.wireOp",EDGE,"E58"),sQuery(id+"F2.wireOp",EDGE,"E61"),sQuery(id+"F2.wireOp",EDGE,"E63"),sQuery(id+"F2.wireOp",EDGE,"E64"),sQuery(id+"F2.wireOp",EDGE,"E67"),sQuery(id+"F2.wireOp",EDGE,"E69"),sQuery(id+"F2.wireOp",EDGE,"E70"),sQuery(id+"F2.wireOp",EDGE,"E73"),sQuery(id+"F2.wireOp",EDGE,"E74"),sQuery(id+"F2.wireOp",EDGE,"E75"),sQuery(id+"F2.wireOp",EDGE,"E76.1.0.0"),sQuery(id+"F2.wireOp",EDGE,"E76.2.0.0"),sQuery(id+"F2.wireOp",EDGE,"E76.3.0.0"),sQuery(id+"F2.wireOp",EDGE,"E76.4.0.0"),sQuery(id+"F2.wireOp",EDGE,"E76.5.0.0"),sQuery(id+"F2.wireOp",EDGE,"E77"),sQuery(id+"F2.wireOp",EDGE,"E79"),sQuery(id+"F2.wireOp",EDGE,"E1"),sQuery(id+"F2.wireOp",EDGE,"E80.1.0.0"),sQuery(id+"F2.wireOp",EDGE,"E80.2.0.0"),sQuery(id+"F2.wireOp",EDGE,"E80.3.0.0"),sQuery(id+"F2.wireOp",EDGE,"E80.4.0.0"),sQuery(id+"F2.wireOp",EDGE,"E81"),sQuery(id+"F2.wireOp",EDGE,"E82"),sQuery(id+"F2.wireOp",EDGE,"E83"),sQuery(id+"F2.wireOp",EDGE,"E84"),sQuery(id+"F2.wireOp",EDGE,"E85"),sQuery(id+"F2.wireOp",EDGE,"E86"),sQuery(id+"F2.wireOp",EDGE,"E87"),sQuery(id+"F2.wireOp",EDGE,"E88"),sQuery(id+"F2.wireOp",EDGE,"E89"),sQuery(id+"F2.wireOp",EDGE,"E90"),sQuery(id+"F2.wireOp",EDGE,"E91"),sQuery(id+"F2.wireOp",EDGE,"E92"),sQuery(id+"F2.wireOp",EDGE,"E93"),sQuery(id+"F2.wireOp",EDGE,"E94"),sQuery(id+"F2.wireOp",EDGE,"E95"),sQuery(id+"F2.wireOp",EDGE,"E96"),sQuery(id+"F2.wireOp",EDGE,"E97"),sQuery(id+"F2.wireOp",EDGE,"E98"),sQuery(id+"F2.wireOp",EDGE,"E99"),sQuery(id+"F2.wireOp",EDGE,"E100"),sQuery(id+"F2.wireOp",EDGE,"E101"),sQuery(id+"F2.wireOp",EDGE,"E102"),sQuery(id+"F2.wireOp",EDGE,"E103"),sQuery(id+"F2.wireOp",EDGE,"E104"),sQuery(id+"F2.wireOp",EDGE,"E105"),sQuery(id+"F2.wireOp",EDGE,"E106"),sQuery(id+"F2.wireOp",EDGE,"E107"),sQuery(id+"F2.wireOp",EDGE,"E108"),sQuery(id+"F2.wireOp",EDGE,"E109"),sQuery(id+"F2.wireOp",EDGE,"E110"),sQuery(id+"F2.wireOp",EDGE,"E111"),sQuery(id+"F2.wireOp",EDGE,"E112"),sQuery(id+"F2.wireOp",EDGE,"E113"),sQuery(id+"F2.wireOp",EDGE,"E114"),sQuery(id+"F2.wireOp",EDGE,"E115"),sQuery(id+"F2.wireOp",EDGE,"E116"),sQuery(id+"F2.wireOp",EDGE,"E117"),sQuery(id+"F2.wireOp",EDGE,"E118"),sQuery(id+"F2.wireOp",EDGE,"E119"),sQuery(id+"F2.wireOp",EDGE,"E120"),sQuery(id+"F2.wireOp",EDGE,"E121"),sQuery(id+"F2.wireOp",EDGE,"E122"),sQuery(id+"F2.wireOp",EDGE,"E123"),sQuery(id+"F2.wireOp",EDGE,"E124"),sQuery(id+"F2.wireOp",EDGE,"E125"),sQuery(id+"F2.wireOp",EDGE,"E126"),sQuery(id+"F2.wireOp",EDGE,"E127"),sQuery(id+"F2.wireOp",EDGE,"E128"),sQuery(id+"F2.wireOp",EDGE,"E129"),sQuery(id+"F2.wireOp",EDGE,"E130"),sQuery(id+"F2.wireOp",EDGE,"E131"),sQuery(id+"F2.wireOp",EDGE,"E132"),sQuery(id+"F2.wireOp",EDGE,"E133"),sQuery(id+"F2.wireOp",EDGE,"E134"),sQuery(id+"F2.wireOp",EDGE,"E135"),sQuery(id+"F2.wireOp",EDGE,"E136"),sQuery(id+"F2.wireOp",EDGE,"E137"),sQuery(id+"F2.wireOp",EDGE,"E138"),sQuery(id+"F2.wireOp",EDGE,"E139"),sQuery(id+"F2.wireOp",EDGE,"E140"),sQuery(id+"F2.wireOp",EDGE,"E141"),sQuery(id+"F2.wireOp",EDGE,"E142"),sQuery(id+"F2.wireOp",EDGE,"E143"),sQuery(id+"F2.wireOp",EDGE,"E144"),sQuery(id+"F2.wireOp",EDGE,"E145"),sQuery(id+"F2.wireOp",EDGE,"E146"),sQuery(id+"F2.wireOp",EDGE,"E147"),sQuery(id+"F2.wireOp",EDGE,"E148"),sQuery(id+"F2.wireOp",EDGE,"E149"),sQuery(id+"F2.wireOp",EDGE,"E150"),sQuery(id+"F2.wireOp",EDGE,"E151"),sQuery(id+"F2.wireOp",EDGE,"E152"),sQuery(id+"F2.wireOp",EDGE,"E153"),sQuery(id+"F2.wireOp",EDGE,"E154"),sQuery(id+"F2.wireOp",EDGE,"E155"),sQuery(id+"F2.wireOp",EDGE,"E156"),sQuery(id+"F2.wireOp",EDGE,"E157"),sQuery(id+"F2.wireOp",EDGE,"E158")])],"isStart":false});
            var sketch = newSketch(context, id + "F4", { "sketchPlane" : qUnion([Q0])});
            skText(sketch, "E159", { "text": "1", "fontName": "OpenSans-Bold.ttf"});
            skText(sketch, "E160", { "text": "2", "fontName": "OpenSans-Bold.ttf"});
            skText(sketch, "E161", { "text": "3", "fontName": "OpenSans-Bold.ttf"});
            skText(sketch, "E162", { "text": "4", "fontName": "OpenSans-Bold.ttf"});
            skText(sketch, "E163", { "text": "5", "fontName": "OpenSans-Bold.ttf"});
            skText(sketch, "E164", { "text": "6", "fontName": "OpenSans-Bold.ttf"});
            const initialGuessF4  = {"E159": [-0.05402, 0, 1, 0, 0.00482], "E160": [-0.0294, 0, 1, 0, 0.00477], "E161": [-0.0038, 0, 1, 0, 0.00458], "E162": [0.0213, 0, 1, 0, 0.00472], "E163": [0.04695, 0, 1, 0, 0.00474], "E164": [0.07223, 0, 1, 0, 0.00474]};
            skSetInitialGuess(sketch, initialGuessF4);
            skSolve(sketch);
        }
        {
            var Q0;
            Q0 = qSketchRegion(id + "F4", true);
            var Q1;
            Q1 = qConstructionFilter(qBodyType(qCreatedBy(id + "F4" ,EDGE), BodyType.WIRE), ConstructionObject.NO);
            extrude(context, id + "F5", {"entities" : qUnion([Q0]), "operationType" : NewBodyOperationType.REMOVE, "surfaceEntities" : qUnion([Q1]), "oppositeDirection" : true, "depth" : 1.59 * mm, "offsetDistance" : 25.4 * mm});
        }
    });
